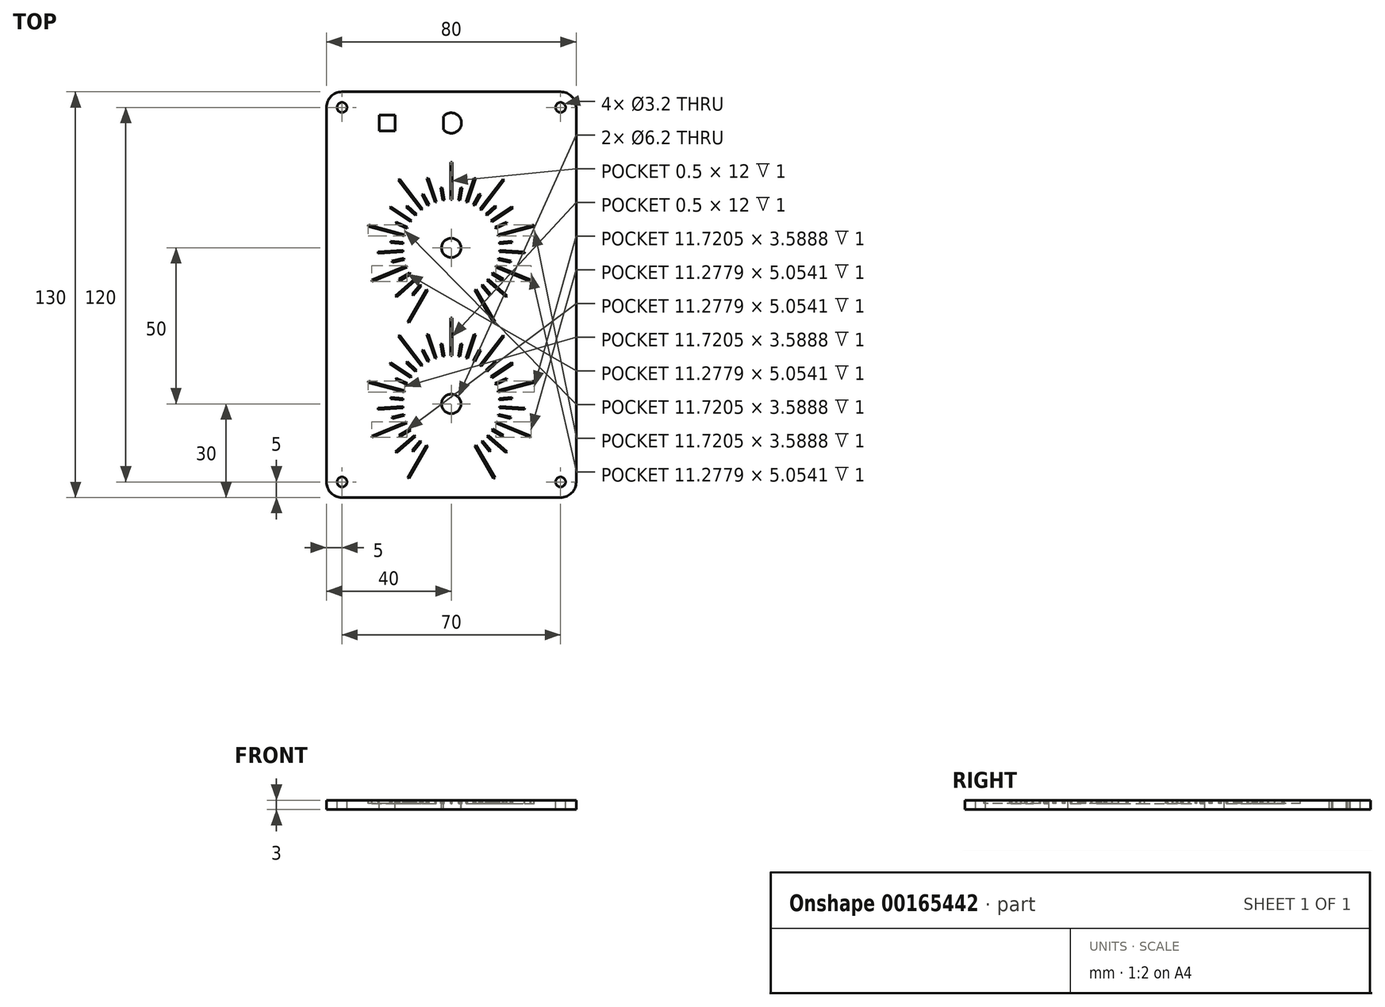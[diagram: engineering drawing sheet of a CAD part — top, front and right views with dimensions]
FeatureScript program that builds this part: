
annotation { "Feature Type Name" : "Feature", "Feature Type Description" : "" }
export const myFeature = defineFeature(function(context is Context, id is Id, definition is map)
    precondition{}
    {
        {
            var Q0;
            Q0=qCreatedBy(makeId("Top.planeOp"),FACE);
            var sketch = newSketch(context, id + "F0", { "sketchPlane" : qUnion([Q0])});
            skLineSegment(sketch, "E0.bottom", {"start": v(-35, 65) * mm, "end": v(35, 65) * mm});
            skLineSegment(sketch, "E0.top", {"start": v(-35, -65) * mm, "end": v(35, -65) * mm});
            skLineSegment(sketch, "E0.left", {"start": v(-40, 60) * mm, "end": v(-40, -60) * mm});
            skLineSegment(sketch, "E0.right", {"start": v(40, 60) * mm, "end": v(40, -60) * mm});
            skPoint(sketch, "E1", {"position": v(-40, 0) * mm});
            skPoint(sketch, "E2", {"position": v(0, 65) * mm});
            skPoint(sketch, "E3.visualSharp", {"position": v(-40, 65) * mm});
            skArc(sketch, "E3.filletArc", {"start": v(-35, 65) * mm, "mid": v(-38.54, 63.54) * mm, "end": v(-40, 60) * mm});
            skPoint(sketch, "E4.visualSharp", {"position": v(40, 65) * mm});
            skArc(sketch, "E4.filletArc", {"start": v(40, 60) * mm, "mid": v(38.54, 63.54) * mm, "end": v(35, 65) * mm});
            skPoint(sketch, "E5.visualSharp", {"position": v(-40, -65) * mm});
            skArc(sketch, "E5.filletArc", {"start": v(-40, -60) * mm, "mid": v(-38.54, -63.54) * mm, "end": v(-35, -65) * mm});
            skPoint(sketch, "E6.visualSharp", {"position": v(40, -65) * mm});
            skArc(sketch, "E6.filletArc", {"start": v(35, -65) * mm, "mid": v(38.54, -63.54) * mm, "end": v(40, -60) * mm});
            skSolve(sketch);
        }
        {
            var Q0;
            Q0=qSketchRegion(id+"F0",true);
            extrude(context, id + "F1", {"entities" : qUnion([Q0]), "depth" : 3 * mm});
        }
        {
            var Q0;
            Q0=makeQuery(id+"F1.opExtrude","CAP_FACE",FACE,{"disambiguationData":[OSD([sQuery(id+"F0.wireOp",EDGE,"E0.bottom"),sQuery(id+"F0.wireOp",EDGE,"E0.top"),sQuery(id+"F0.wireOp",EDGE,"E0.left"),sQuery(id+"F0.wireOp",EDGE,"E0.right"),sQuery(id+"F0.wireOp",EDGE,"E3.filletArc"),sQuery(id+"F0.wireOp",EDGE,"E4.filletArc"),sQuery(id+"F0.wireOp",EDGE,"E5.filletArc"),sQuery(id+"F0.wireOp",EDGE,"E6.filletArc")])],"isStart":false});
            var sketch = newSketch(context, id + "F2", { "sketchPlane" : qUnion([Q0])});
            skCircle(sketch, "E7", {"center": v(0, 15) * mm, "radius": 3.1 * mm});
            skCircle(sketch, "E8", {"center": v(0, -35) * mm, "radius": 3.1 * mm});
            skCircle(sketch, "E9", {"center": v(0, 15) * mm, "radius": 15.5 * mm, "construction": true});
            skCircle(sketch, "E10", {"center": v(0, -35) * mm, "radius": 15.5 * mm, "construction": true});
            skSolve(sketch);
        }
        {
            var Q0;
            Q0=qSketchRegion(id+"F2",true);
            extrude(context, id + "F3", {"entities" : qUnion([Q0]), "operationType" : NewBodyOperationType.REMOVE, "endBound" : BoundingType.THROUGH_ALL, "oppositeDirection" : true, "depth" : 25 * mm});
        }
        {
            var Q0;
            Q0=makeQuery(id+"F1.opExtrude","CAP_FACE",FACE,{"disambiguationData":[OSD([sQuery(id+"F0.wireOp",EDGE,"E0.bottom"),sQuery(id+"F0.wireOp",EDGE,"E0.top"),sQuery(id+"F0.wireOp",EDGE,"E0.left"),sQuery(id+"F0.wireOp",EDGE,"E0.right"),sQuery(id+"F0.wireOp",EDGE,"E3.filletArc"),sQuery(id+"F0.wireOp",EDGE,"E4.filletArc"),sQuery(id+"F0.wireOp",EDGE,"E5.filletArc"),sQuery(id+"F0.wireOp",EDGE,"E6.filletArc")])],"isStart":false});
            var sketch = newSketch(context, id + "F4", { "sketchPlane" : qUnion([Q0])});
            skLineSegment(sketch, "E11", {"start": v(0, 15) * mm, "end": v(0, -35) * mm, "construction": true});
            skCircle(sketch, "E12", {"center": v(-35, 60) * mm, "radius": 1.6 * mm});
            skCircle(sketch, "E13", {"center": v(35, 60) * mm, "radius": 1.6 * mm});
            skCircle(sketch, "E14", {"center": v(35, -60) * mm, "radius": 1.6 * mm});
            skCircle(sketch, "E15", {"center": v(-35, -60) * mm, "radius": 1.6 * mm});
            skSolve(sketch);
        }
        {
            var Q0;
            Q0=qSketchRegion(id+"F4",true);
            extrude(context, id + "F5", {"entities" : qUnion([Q0]), "operationType" : NewBodyOperationType.REMOVE, "endBound" : BoundingType.THROUGH_ALL, "oppositeDirection" : true, "depth" : 25 * mm});
        }
        {
            var Q0;
            Q0=makeQuery(id+"F2.imprint","IMPRINT",FACE,{"disambiguationData":[TD([[makeQuery(id+"F2.imprint","IMPRINT",EDGE,{"derivedFrom":sQuery(id+"F2.wireOp",EDGE,"E7")}),-1.0]])]});
            var sketch = newSketch(context, id + "F6", { "sketchPlane" : qUnion([Q0])});
            skArc(sketch, "E16", {"start": v(-2.46, 52.85) * mm, "mid": v(3.26, 55) * mm, "end": v(-2.46, 57.15) * mm});
            skLineSegment(sketch, "E17", {"start": v(-2.46, 57.15) * mm, "end": v(-2.46, 52.85) * mm});
            skLineSegment(sketch, "E18.bottom", {"start": v(-23.1, 57.55) * mm, "end": v(-18, 57.55) * mm});
            skLineSegment(sketch, "E18.top", {"start": v(-23.1, 52.45) * mm, "end": v(-18, 52.45) * mm});
            skLineSegment(sketch, "E18.left", {"start": v(-23.1, 57.55) * mm, "end": v(-23.1, 52.45) * mm});
            skLineSegment(sketch, "E18.right", {"start": v(-18, 57.55) * mm, "end": v(-18, 52.45) * mm});
            skPoint(sketch, "E19", {"position": v(-23.1, 55) * mm});
            skSolve(sketch);
        }
        {
            var Q0;
            Q0 = qSketchRegion(id + "F6", true);
            extrude(context, id + "F7", {"entities" : qUnion([Q0]), "operationType" : NewBodyOperationType.REMOVE, "endBound" : BoundingType.THROUGH_ALL, "oppositeDirection" : true, "depth" : 25 * mm});
        }
        {
            var Q0;
            Q0=makeQuery(id+"F2.imprint","IMPRINT",FACE,{"disambiguationData":[TD([[makeQuery(id+"F2.imprint","IMPRINT",EDGE,{"derivedFrom":sQuery(id+"F2.wireOp",EDGE,"E7")}),-1.0]])]});
            var sketch = newSketch(context, id + "F8", { "sketchPlane" : qUnion([Q0])});
            skLineSegment(sketch, "E20.bottom", {"start": v(-0.25, 34.5) * mm, "end": v(0.25, 34.5) * mm});
            skLineSegment(sketch, "E20.top", {"start": v(-0.25, 30.5) * mm, "end": v(0.25, 30.5) * mm});
            skLineSegment(sketch, "E20.left", {"start": v(-0.25, 34.5) * mm, "end": v(-0.25, 30.5) * mm});
            skLineSegment(sketch, "E20.right", {"start": v(0.25, 34.5) * mm, "end": v(0.25, 30.5) * mm});
            skLineSegment(sketch, "E21.top", {"start": v(-0.25, 38.5) * mm, "end": v(0.25, 38.5) * mm});
            skLineSegment(sketch, "E21.left", {"start": v(-0.25, 34.5) * mm, "end": v(-0.25, 38.5) * mm});
            skLineSegment(sketch, "E21.right", {"start": v(0.25, 34.5) * mm, "end": v(0.25, 38.5) * mm});
            skLineSegment(sketch, "E22.top", {"start": v(-0.25, 42.5) * mm, "end": v(0.25, 42.5) * mm});
            skLineSegment(sketch, "E22.left", {"start": v(-0.25, 38.5) * mm, "end": v(-0.25, 42.5) * mm});
            skLineSegment(sketch, "E22.right", {"start": v(0.25, 38.5) * mm, "end": v(0.25, 42.5) * mm});
            skPoint(sketch, "E23", {"position": v(0, 30.5) * mm});
            skLineSegment(sketch, "E24.1.0", {"start": v(14.1, 33.8) * mm, "end": v(16.54, 36.97) * mm});
            skLineSegment(sketch, "E24.1.1", {"start": v(16.54, 36.97) * mm, "end": v(16.94, 36.66) * mm});
            skLineSegment(sketch, "E24.1.2", {"start": v(14.1, 33.8) * mm, "end": v(14.5, 33.5) * mm});
            skLineSegment(sketch, "E24.1.3", {"start": v(14.5, 33.5) * mm, "end": v(16.94, 36.66) * mm});
            skLineSegment(sketch, "E24.1.4", {"start": v(14.1, 33.8) * mm, "end": v(14.5, 33.5) * mm});
            skLineSegment(sketch, "E24.2.0", {"start": v(22.63, 21.32) * mm, "end": v(26.5, 22.36) * mm});
            skLineSegment(sketch, "E24.2.1", {"start": v(26.5, 22.36) * mm, "end": v(26.63, 21.88) * mm});
            skLineSegment(sketch, "E24.2.2", {"start": v(22.63, 21.32) * mm, "end": v(22.76, 20.84) * mm});
            skLineSegment(sketch, "E24.2.3", {"start": v(22.76, 20.84) * mm, "end": v(26.63, 21.88) * mm});
            skLineSegment(sketch, "E24.2.4", {"start": v(22.63, 21.32) * mm, "end": v(22.76, 20.84) * mm});
            skPoint(sketch, "E24.center", {"position": v(0, 15) * mm});
            skLineSegment(sketch, "E24.anchor1", {"start": v(0, 15) * mm, "end": v(-0.25, 38.5) * mm, "construction": true});
            skLineSegment(sketch, "E24.anchor2", {"start": v(0, 15) * mm, "end": v(11.97, -5.22) * mm, "construction": true});
            skLineSegment(sketch, "E25.1.3.0", {"start": v(21.8, 6.24) * mm, "end": v(25.5, 4.7) * mm});
            skLineSegment(sketch, "E25.3.3.0", {"start": v(25.5, 4.7) * mm, "end": v(25.3, 4.25) * mm});
            skLineSegment(sketch, "E25.6.3.0", {"start": v(21.8, 6.24) * mm, "end": v(21.61, 5.78) * mm});
            skLineSegment(sketch, "E25.9.3.0", {"start": v(21.61, 5.78) * mm, "end": v(25.3, 4.25) * mm});
            skLineSegment(sketch, "E25.12.3.0", {"start": v(21.8, 6.24) * mm, "end": v(21.61, 5.78) * mm});
            skLineSegment(sketch, "E25.1.4.0", {"start": v(11.97, -5.22) * mm, "end": v(13.97, -8.69) * mm});
            skLineSegment(sketch, "E25.3.4.0", {"start": v(13.97, -8.69) * mm, "end": v(13.53, -8.94) * mm});
            skLineSegment(sketch, "E25.6.4.0", {"start": v(11.97, -5.22) * mm, "end": v(11.53, -5.47) * mm});
            skLineSegment(sketch, "E25.9.4.0", {"start": v(11.53, -5.47) * mm, "end": v(13.53, -8.94) * mm});
            skLineSegment(sketch, "E25.12.4.0", {"start": v(11.97, -5.22) * mm, "end": v(11.53, -5.47) * mm});
            skLineSegment(sketch, "E26.1.0", {"start": v(7.32, 37.33) * mm, "end": v(7.79, 37.17) * mm});
            skLineSegment(sketch, "E26.1.1", {"start": v(6.5, 33.38) * mm, "end": v(7.79, 37.17) * mm});
            skLineSegment(sketch, "E26.1.2", {"start": v(6.03, 33.54) * mm, "end": v(6.5, 33.38) * mm});
            skLineSegment(sketch, "E26.1.3", {"start": v(6.03, 33.54) * mm, "end": v(7.32, 37.33) * mm});
            skLineSegment(sketch, "E26.1.4", {"start": v(7.32, 37.33) * mm, "end": v(7.79, 37.17) * mm});
            skLineSegment(sketch, "E26.1.5", {"start": v(6.03, 33.54) * mm, "end": v(6.5, 33.38) * mm});
            skLineSegment(sketch, "E26.2.1", {"start": v(12.07, 30.32) * mm, "end": v(14.5, 33.5) * mm});
            skLineSegment(sketch, "E26.2.2", {"start": v(11.67, 30.62) * mm, "end": v(12.07, 30.32) * mm});
            skLineSegment(sketch, "E26.2.3", {"start": v(11.67, 30.62) * mm, "end": v(14.1, 33.8) * mm});
            skLineSegment(sketch, "E26.2.5", {"start": v(11.67, 30.62) * mm, "end": v(12.07, 30.32) * mm});
            skLineSegment(sketch, "E26.3.0", {"start": v(19.4, 28.26) * mm, "end": v(19.68, 27.85) * mm});
            skLineSegment(sketch, "E26.3.1", {"start": v(16.35, 25.62) * mm, "end": v(19.68, 27.85) * mm});
            skLineSegment(sketch, "E26.3.2", {"start": v(16.07, 26.04) * mm, "end": v(16.35, 25.62) * mm});
            skLineSegment(sketch, "E26.3.3", {"start": v(16.07, 26.04) * mm, "end": v(19.4, 28.26) * mm});
            skLineSegment(sketch, "E26.3.4", {"start": v(19.4, 28.26) * mm, "end": v(19.68, 27.85) * mm});
            skLineSegment(sketch, "E26.3.5", {"start": v(16.07, 26.04) * mm, "end": v(16.35, 25.62) * mm});
            skLineSegment(sketch, "E26.4.1", {"start": v(18.9, 19.8) * mm, "end": v(22.76, 20.84) * mm});
            skLineSegment(sketch, "E26.4.2", {"start": v(18.77, 20.29) * mm, "end": v(18.9, 19.8) * mm});
            skLineSegment(sketch, "E26.4.3", {"start": v(18.77, 20.29) * mm, "end": v(22.63, 21.32) * mm});
            skLineSegment(sketch, "E26.4.5", {"start": v(18.77, 20.29) * mm, "end": v(18.9, 19.8) * mm});
            skLineSegment(sketch, "E26.5.0", {"start": v(23.46, 13.71) * mm, "end": v(23.43, 13.21) * mm});
            skLineSegment(sketch, "E26.5.1", {"start": v(19.44, 13.48) * mm, "end": v(23.43, 13.21) * mm});
            skLineSegment(sketch, "E26.5.2", {"start": v(19.47, 13.97) * mm, "end": v(19.44, 13.48) * mm});
            skLineSegment(sketch, "E26.5.3", {"start": v(19.47, 13.97) * mm, "end": v(23.46, 13.71) * mm});
            skLineSegment(sketch, "E26.5.4", {"start": v(23.46, 13.71) * mm, "end": v(23.43, 13.21) * mm});
            skLineSegment(sketch, "E26.5.5", {"start": v(19.47, 13.97) * mm, "end": v(19.44, 13.48) * mm});
            skLineSegment(sketch, "E26.6.1", {"start": v(17.92, 7.3) * mm, "end": v(21.61, 5.78) * mm});
            skLineSegment(sketch, "E26.6.2", {"start": v(18.1, 7.77) * mm, "end": v(17.92, 7.3) * mm});
            skLineSegment(sketch, "E26.6.3", {"start": v(18.1, 7.77) * mm, "end": v(21.8, 6.24) * mm});
            skLineSegment(sketch, "E26.6.5", {"start": v(18.1, 7.77) * mm, "end": v(17.92, 7.3) * mm});
            skLineSegment(sketch, "E26.7.0", {"start": v(17.83, -0.3) * mm, "end": v(17.5, -0.68) * mm});
            skLineSegment(sketch, "E26.7.1", {"start": v(14.5, 1.96) * mm, "end": v(17.5, -0.68) * mm});
            skLineSegment(sketch, "E26.7.2", {"start": v(14.82, 2.33) * mm, "end": v(14.5, 1.96) * mm});
            skLineSegment(sketch, "E26.7.3", {"start": v(14.82, 2.33) * mm, "end": v(17.83, -0.3) * mm});
            skLineSegment(sketch, "E26.7.4", {"start": v(17.83, -0.3) * mm, "end": v(17.5, -0.68) * mm});
            skLineSegment(sketch, "E26.7.5", {"start": v(14.82, 2.33) * mm, "end": v(14.5, 1.96) * mm});
            skLineSegment(sketch, "E26.8.1", {"start": v(9.53, -2.01) * mm, "end": v(11.53, -5.47) * mm});
            skLineSegment(sketch, "E26.8.2", {"start": v(9.97, -1.76) * mm, "end": v(9.53, -2.01) * mm});
            skLineSegment(sketch, "E26.8.3", {"start": v(9.97, -1.76) * mm, "end": v(11.97, -5.22) * mm});
            skLineSegment(sketch, "E26.8.5", {"start": v(9.97, -1.76) * mm, "end": v(9.53, -2.01) * mm});
            skLineSegment(sketch, "E26.anchor1", {"start": v(0, 15) * mm, "end": v(-0.25, 34.5) * mm, "construction": true});
            skLineSegment(sketch, "E26.anchor2", {"start": v(0, 15) * mm, "end": v(9.97, -1.76) * mm, "construction": true});
            skPoint(sketch, "E27.1.0", {"position": v(2.52, 30.3) * mm});
            skLineSegment(sketch, "E27.1.1", {"start": v(3.42, 34.2) * mm, "end": v(2.77, 30.25) * mm});
            skLineSegment(sketch, "E27.1.2", {"start": v(2.93, 34.28) * mm, "end": v(3.42, 34.2) * mm});
            skLineSegment(sketch, "E27.1.3", {"start": v(2.93, 34.28) * mm, "end": v(2.28, 30.33) * mm});
            skLineSegment(sketch, "E27.1.4", {"start": v(2.93, 34.28) * mm, "end": v(3.42, 34.2) * mm});
            skLineSegment(sketch, "E27.1.5", {"start": v(2.28, 30.33) * mm, "end": v(2.77, 30.25) * mm});
            skPoint(sketch, "E27.2.0", {"position": v(4.98, 29.68) * mm});
            skLineSegment(sketch, "E27.2.1", {"start": v(6.5, 33.38) * mm, "end": v(5.22, 29.6) * mm});
            skLineSegment(sketch, "E27.2.3", {"start": v(6.03, 33.54) * mm, "end": v(4.74, 29.76) * mm});
            skLineSegment(sketch, "E27.2.5", {"start": v(4.74, 29.76) * mm, "end": v(5.22, 29.6) * mm});
            skPoint(sketch, "E27.3.0", {"position": v(7.3, 28.67) * mm});
            skLineSegment(sketch, "E27.3.1", {"start": v(9.41, 32.08) * mm, "end": v(7.53, 28.55) * mm});
            skLineSegment(sketch, "E27.3.2", {"start": v(8.97, 32.31) * mm, "end": v(9.41, 32.08) * mm});
            skLineSegment(sketch, "E27.3.3", {"start": v(8.97, 32.31) * mm, "end": v(7.09, 28.79) * mm});
            skLineSegment(sketch, "E27.3.4", {"start": v(8.97, 32.31) * mm, "end": v(9.41, 32.08) * mm});
            skLineSegment(sketch, "E27.3.5", {"start": v(7.09, 28.79) * mm, "end": v(7.53, 28.55) * mm});
            skPoint(sketch, "E27.4.0", {"position": v(9.43, 27.3) * mm});
            skLineSegment(sketch, "E27.4.1", {"start": v(12.07, 30.32) * mm, "end": v(9.63, 27.14) * mm});
            skLineSegment(sketch, "E27.4.3", {"start": v(11.67, 30.62) * mm, "end": v(9.24, 27.45) * mm});
            skLineSegment(sketch, "E27.4.5", {"start": v(9.24, 27.45) * mm, "end": v(9.63, 27.14) * mm});
            skPoint(sketch, "E27.5.0", {"position": v(11.31, 25.6) * mm});
            skLineSegment(sketch, "E27.5.1", {"start": v(14.4, 28.15) * mm, "end": v(11.48, 25.41) * mm});
            skLineSegment(sketch, "E27.5.2", {"start": v(14.06, 28.51) * mm, "end": v(14.4, 28.15) * mm});
            skLineSegment(sketch, "E27.5.3", {"start": v(14.06, 28.51) * mm, "end": v(11.14, 25.78) * mm});
            skLineSegment(sketch, "E27.5.4", {"start": v(14.06, 28.51) * mm, "end": v(14.4, 28.15) * mm});
            skLineSegment(sketch, "E27.5.5", {"start": v(11.14, 25.78) * mm, "end": v(11.48, 25.41) * mm});
            skPoint(sketch, "E27.6.0", {"position": v(12.89, 23.61) * mm});
            skLineSegment(sketch, "E27.6.1", {"start": v(16.35, 25.62) * mm, "end": v(13.02, 23.4) * mm});
            skLineSegment(sketch, "E27.6.3", {"start": v(16.07, 26.04) * mm, "end": v(12.75, 23.82) * mm});
            skLineSegment(sketch, "E27.6.5", {"start": v(12.75, 23.82) * mm, "end": v(13.02, 23.4) * mm});
            skPoint(sketch, "E27.7.0", {"position": v(14.12, 21.4) * mm});
            skLineSegment(sketch, "E27.7.1", {"start": v(17.86, 22.82) * mm, "end": v(14.22, 21.17) * mm});
            skLineSegment(sketch, "E27.7.2", {"start": v(17.66, 23.27) * mm, "end": v(17.86, 22.82) * mm});
            skLineSegment(sketch, "E27.7.3", {"start": v(17.66, 23.27) * mm, "end": v(14.01, 21.62) * mm});
            skLineSegment(sketch, "E27.7.4", {"start": v(17.66, 23.27) * mm, "end": v(17.86, 22.82) * mm});
            skLineSegment(sketch, "E27.7.5", {"start": v(14.01, 21.62) * mm, "end": v(14.22, 21.17) * mm});
            skPoint(sketch, "E27.8.0", {"position": v(14.97, 19.01) * mm});
            skLineSegment(sketch, "E27.8.1", {"start": v(18.9, 19.8) * mm, "end": v(15.03, 18.77) * mm});
            skLineSegment(sketch, "E27.8.3", {"start": v(18.77, 20.29) * mm, "end": v(14.9, 19.25) * mm});
            skLineSegment(sketch, "E27.8.5", {"start": v(14.9, 19.25) * mm, "end": v(15.03, 18.77) * mm});
            skPoint(sketch, "E27.9.0", {"position": v(15.42, 16.52) * mm});
            skLineSegment(sketch, "E27.9.1", {"start": v(19.43, 16.66) * mm, "end": v(15.45, 16.27) * mm});
            skLineSegment(sketch, "E27.9.2", {"start": v(19.38, 17.16) * mm, "end": v(19.43, 16.66) * mm});
            skLineSegment(sketch, "E27.9.3", {"start": v(19.38, 17.16) * mm, "end": v(15.4, 16.77) * mm});
            skLineSegment(sketch, "E27.9.4", {"start": v(19.38, 17.16) * mm, "end": v(19.43, 16.66) * mm});
            skLineSegment(sketch, "E27.9.5", {"start": v(15.4, 16.77) * mm, "end": v(15.45, 16.27) * mm});
            skPoint(sketch, "E27.10.0", {"position": v(15.46, 13.99) * mm});
            skLineSegment(sketch, "E27.10.1", {"start": v(19.44, 13.48) * mm, "end": v(15.45, 13.74) * mm});
            skLineSegment(sketch, "E27.10.3", {"start": v(19.47, 13.97) * mm, "end": v(15.48, 14.24) * mm});
            skLineSegment(sketch, "E27.10.5", {"start": v(15.48, 14.24) * mm, "end": v(15.45, 13.74) * mm});
            skPoint(sketch, "E27.11.0", {"position": v(15.1, 11.48) * mm});
            skLineSegment(sketch, "E27.11.1", {"start": v(18.93, 10.33) * mm, "end": v(15.04, 11.24) * mm});
            skLineSegment(sketch, "E27.11.2", {"start": v(19.05, 10.82) * mm, "end": v(18.93, 10.33) * mm});
            skLineSegment(sketch, "E27.11.3", {"start": v(19.05, 10.82) * mm, "end": v(15.15, 11.72) * mm});
            skLineSegment(sketch, "E27.11.4", {"start": v(19.05, 10.82) * mm, "end": v(18.93, 10.33) * mm});
            skLineSegment(sketch, "E27.11.5", {"start": v(15.15, 11.72) * mm, "end": v(15.04, 11.24) * mm});
            skPoint(sketch, "E27.12.0", {"position": v(14.32, 9.07) * mm});
            skLineSegment(sketch, "E27.12.1", {"start": v(17.92, 7.3) * mm, "end": v(14.22, 8.84) * mm});
            skLineSegment(sketch, "E27.12.3", {"start": v(18.1, 7.77) * mm, "end": v(14.41, 9.3) * mm});
            skLineSegment(sketch, "E27.12.5", {"start": v(14.41, 9.3) * mm, "end": v(14.22, 8.84) * mm});
            skPoint(sketch, "E27.13.0", {"position": v(13.16, 6.82) * mm});
            skLineSegment(sketch, "E27.13.1", {"start": v(16.43, 4.5) * mm, "end": v(13.03, 6.6) * mm});
            skLineSegment(sketch, "E27.13.2", {"start": v(16.69, 4.92) * mm, "end": v(16.43, 4.5) * mm});
            skLineSegment(sketch, "E27.13.3", {"start": v(16.69, 4.92) * mm, "end": v(13.3, 7.03) * mm});
            skLineSegment(sketch, "E27.13.4", {"start": v(16.69, 4.92) * mm, "end": v(16.43, 4.5) * mm});
            skLineSegment(sketch, "E27.13.5", {"start": v(13.3, 7.03) * mm, "end": v(13.03, 6.6) * mm});
            skPoint(sketch, "E27.14.0", {"position": v(11.65, 4.78) * mm});
            skLineSegment(sketch, "E27.14.1", {"start": v(14.5, 1.96) * mm, "end": v(11.49, 4.6) * mm});
            skLineSegment(sketch, "E27.14.3", {"start": v(14.82, 2.33) * mm, "end": v(11.82, 4.97) * mm});
            skLineSegment(sketch, "E27.14.5", {"start": v(11.82, 4.97) * mm, "end": v(11.49, 4.6) * mm});
            skPoint(sketch, "E27.15.0", {"position": v(9.83, 3.02) * mm});
            skLineSegment(sketch, "E27.15.1", {"start": v(12.18, -0.23) * mm, "end": v(9.64, 2.86) * mm});
            skLineSegment(sketch, "E27.15.2", {"start": v(12.56, 0.09) * mm, "end": v(12.18, -0.23) * mm});
            skLineSegment(sketch, "E27.15.3", {"start": v(12.56, 0.09) * mm, "end": v(10.03, 3.18) * mm});
            skLineSegment(sketch, "E27.15.4", {"start": v(12.56, 0.09) * mm, "end": v(12.18, -0.23) * mm});
            skLineSegment(sketch, "E27.15.5", {"start": v(10.03, 3.18) * mm, "end": v(9.64, 2.86) * mm});
            skLineSegment(sketch, "E27.anchor1", {"start": v(0, 15) * mm, "end": v(-0.25, 30.5) * mm, "construction": true});
            skLineSegment(sketch, "E27.anchor2", {"start": v(0, 15) * mm, "end": v(7.97, 1.7) * mm, "construction": true});
            skLineSegment(sketch, "E28.1.16.0", {"start": v(9.53, -2.01) * mm, "end": v(7.53, 1.45) * mm});
            skLineSegment(sketch, "E28.7.16.0", {"start": v(9.97, -1.76) * mm, "end": v(7.97, 1.7) * mm});
            skPoint(sketch, "E28.9.16.0", {"position": v(7.75, 1.58) * mm});
            skLineSegment(sketch, "E28.13.16.0", {"start": v(7.97, 1.7) * mm, "end": v(7.53, 1.45) * mm});
            skLineSegment(sketch, "E29.MirrorCS", {"start": v(-9.97, -1.76) * mm, "end": v(-9.53, -2.01) * mm});
            skLineSegment(sketch, "E30.MirrorCS", {"start": v(-11.97, -5.22) * mm, "end": v(-11.53, -5.47) * mm});
            skLineSegment(sketch, "E31.MirrorCS", {"start": v(-18.1, 7.77) * mm, "end": v(-17.92, 7.3) * mm});
            skLineSegment(sketch, "E32.MirrorCS", {"start": v(-19.47, 13.97) * mm, "end": v(-19.44, 13.48) * mm});
            skLineSegment(sketch, "E33.MirrorCS", {"start": v(-14.1, 33.8) * mm, "end": v(-14.5, 33.5) * mm});
            skLineSegment(sketch, "E34.MirrorCS", {"start": v(-16.07, 26.04) * mm, "end": v(-16.35, 25.62) * mm});
            skLineSegment(sketch, "E35.MirrorCS", {"start": v(-22.63, 21.32) * mm, "end": v(-22.76, 20.84) * mm});
            skLineSegment(sketch, "E36.MirrorCS", {"start": v(-6.03, 33.54) * mm, "end": v(-6.5, 33.38) * mm});
            skLineSegment(sketch, "E37.MirrorCS", {"start": v(-14.82, 2.33) * mm, "end": v(-14.5, 1.96) * mm});
            skLineSegment(sketch, "E38.MirrorCS", {"start": v(-18.77, 20.29) * mm, "end": v(-18.9, 19.8) * mm});
            skLineSegment(sketch, "E39.MirrorCS", {"start": v(-21.8, 6.24) * mm, "end": v(-21.61, 5.78) * mm});
            skLineSegment(sketch, "E40.MirrorCS", {"start": v(-11.67, 30.62) * mm, "end": v(-12.07, 30.32) * mm});
            skLineSegment(sketch, "E41.MirrorCS", {"start": v(-7.32, 37.33) * mm, "end": v(-7.79, 37.17) * mm});
            skLineSegment(sketch, "E42.MirrorCS", {"start": v(-19.4, 28.26) * mm, "end": v(-19.68, 27.85) * mm});
            skLineSegment(sketch, "E43.MirrorCS", {"start": v(-16.69, 4.92) * mm, "end": v(-16.43, 4.5) * mm});
            skLineSegment(sketch, "E44.MirrorCS", {"start": v(-12.56, 0.09) * mm, "end": v(-12.18, -0.23) * mm});
            skLineSegment(sketch, "E45.MirrorCS", {"start": v(-19.38, 17.16) * mm, "end": v(-19.43, 16.66) * mm});
            skLineSegment(sketch, "E46.MirrorCS", {"start": v(-15.4, 16.77) * mm, "end": v(-15.45, 16.27) * mm});
            skLineSegment(sketch, "E47.MirrorCS", {"start": v(-23.46, 13.71) * mm, "end": v(-23.43, 13.21) * mm});
            skLineSegment(sketch, "E48.MirrorCS", {"start": v(-14.06, 28.51) * mm, "end": v(-14.4, 28.15) * mm});
            skLineSegment(sketch, "E49.MirrorCS", {"start": v(-17.66, 23.27) * mm, "end": v(-17.86, 22.82) * mm});
            skLineSegment(sketch, "E50.MirrorCS", {"start": v(-7.97, 1.7) * mm, "end": v(-7.53, 1.45) * mm});
            skLineSegment(sketch, "E51.MirrorCS", {"start": v(-17.83, -0.3) * mm, "end": v(-17.5, -0.68) * mm});
            skLineSegment(sketch, "E52.MirrorCS", {"start": v(-2.93, 34.28) * mm, "end": v(-3.42, 34.2) * mm});
            skLineSegment(sketch, "E53.MirrorCS", {"start": v(-15.48, 14.24) * mm, "end": v(-15.45, 13.74) * mm});
            skLineSegment(sketch, "E54.MirrorCS", {"start": v(-8.97, 32.31) * mm, "end": v(-9.41, 32.08) * mm});
            skLineSegment(sketch, "E55.MirrorCS", {"start": v(-19.05, 10.82) * mm, "end": v(-18.93, 10.33) * mm});
            skLineSegment(sketch, "E56.MirrorCS", {"start": v(-2.28, 30.33) * mm, "end": v(-2.77, 30.25) * mm});
            skLineSegment(sketch, "E57.MirrorCS", {"start": v(-7.09, 28.79) * mm, "end": v(-7.53, 28.55) * mm});
            skLineSegment(sketch, "E58.MirrorCS", {"start": v(-12.75, 23.82) * mm, "end": v(-13.02, 23.4) * mm});
            skLineSegment(sketch, "E59.MirrorCS", {"start": v(-15.15, 11.72) * mm, "end": v(-15.04, 11.24) * mm});
            skLineSegment(sketch, "E60.MirrorCS", {"start": v(-10.03, 3.18) * mm, "end": v(-9.64, 2.86) * mm});
            skLineSegment(sketch, "E61.MirrorCS", {"start": v(-11.82, 4.97) * mm, "end": v(-11.49, 4.6) * mm});
            skLineSegment(sketch, "E62.MirrorCS", {"start": v(-4.74, 29.76) * mm, "end": v(-5.22, 29.6) * mm});
            skLineSegment(sketch, "E63.MirrorCS", {"start": v(-11.14, 25.78) * mm, "end": v(-11.48, 25.41) * mm});
            skLineSegment(sketch, "E64.MirrorCS", {"start": v(-13.3, 7.03) * mm, "end": v(-13.03, 6.6) * mm});
            skLineSegment(sketch, "E65.MirrorCS", {"start": v(-14.9, 19.25) * mm, "end": v(-15.03, 18.77) * mm});
            skLineSegment(sketch, "E66.MirrorCS", {"start": v(-14.41, 9.3) * mm, "end": v(-14.22, 8.84) * mm});
            skLineSegment(sketch, "E67.MirrorCS", {"start": v(-14.01, 21.62) * mm, "end": v(-14.22, 21.17) * mm});
            skLineSegment(sketch, "E68.MirrorCS", {"start": v(-9.24, 27.45) * mm, "end": v(-9.63, 27.14) * mm});
            skLineSegment(sketch, "E69.MirrorCS", {"start": v(-26.5, 22.36) * mm, "end": v(-26.63, 21.88) * mm});
            skLineSegment(sketch, "E70.MirrorCS", {"start": v(-16.54, 36.97) * mm, "end": v(-16.94, 36.66) * mm});
            skLineSegment(sketch, "E71.MirrorCS", {"start": v(-25.5, 4.7) * mm, "end": v(-25.3, 4.25) * mm});
            skLineSegment(sketch, "E72.MirrorCS", {"start": v(-13.97, -8.69) * mm, "end": v(-13.53, -8.94) * mm});
            skLineSegment(sketch, "E73.MirrorCS", {"start": v(-16.69, 4.92) * mm, "end": v(-13.3, 7.03) * mm});
            skLineSegment(sketch, "E74.MirrorCS", {"start": v(-17.86, 22.82) * mm, "end": v(-14.22, 21.17) * mm});
            skPoint(sketch, "E75.MirrorP", {"position": v(-9.43, 27.3) * mm});
            skLineSegment(sketch, "E76.MirrorCS", {"start": v(-14.5, 33.5) * mm, "end": v(-16.94, 36.66) * mm});
            skLineSegment(sketch, "E77.MirrorCS", {"start": v(-12.07, 30.32) * mm, "end": v(-9.63, 27.14) * mm});
            skLineSegment(sketch, "E78.MirrorCS", {"start": v(-18.1, 7.77) * mm, "end": v(-21.8, 6.24) * mm});
            skLineSegment(sketch, "E79.MirrorCS", {"start": v(-9.97, -1.76) * mm, "end": v(-7.97, 1.7) * mm});
            skLineSegment(sketch, "E80.MirrorCS", {"start": v(-9.53, -2.01) * mm, "end": v(-11.53, -5.47) * mm});
            skLineSegment(sketch, "E81.MirrorCS", {"start": v(-8.97, 32.31) * mm, "end": v(-7.09, 28.79) * mm});
            skLineSegment(sketch, "E82.MirrorCS", {"start": v(-16.07, 26.04) * mm, "end": v(-19.4, 28.26) * mm});
            skLineSegment(sketch, "E83.MirrorCS", {"start": v(-12.07, 30.32) * mm, "end": v(-14.5, 33.5) * mm});
            skLineSegment(sketch, "E84.MirrorCS", {"start": v(-14.82, 2.33) * mm, "end": v(-17.83, -0.3) * mm});
            skLineSegment(sketch, "E85.MirrorCS", {"start": v(-19.47, 13.97) * mm, "end": v(-23.46, 13.71) * mm});
            skPoint(sketch, "E86.MirrorP", {"position": v(-4.98, 29.68) * mm});
            skLineSegment(sketch, "E87.MirrorCS", {"start": v(-17.92, 7.3) * mm, "end": v(-21.61, 5.78) * mm});
            skPoint(sketch, "E88.MirrorP", {"position": v(-13.16, 6.82) * mm});
            skLineSegment(sketch, "E89.MirrorCS", {"start": v(-14.06, 28.51) * mm, "end": v(-11.14, 25.78) * mm});
            skPoint(sketch, "E90.MirrorP", {"position": v(-9.83, 3.02) * mm});
            skLineSegment(sketch, "E91.MirrorCS", {"start": v(-16.35, 25.62) * mm, "end": v(-13.02, 23.4) * mm});
            skLineSegment(sketch, "E92.MirrorCS", {"start": v(-19.44, 13.48) * mm, "end": v(-15.45, 13.74) * mm});
            skLineSegment(sketch, "E93.MirrorCS", {"start": v(-18.1, 7.77) * mm, "end": v(-14.41, 9.3) * mm});
            skLineSegment(sketch, "E94.MirrorCS", {"start": v(-12.18, -0.23) * mm, "end": v(-9.64, 2.86) * mm});
            skLineSegment(sketch, "E95.MirrorCS", {"start": v(-19.43, 16.66) * mm, "end": v(-15.45, 16.27) * mm});
            skLineSegment(sketch, "E96.MirrorCS", {"start": v(-9.53, -2.01) * mm, "end": v(-7.53, 1.45) * mm});
            skLineSegment(sketch, "E97.MirrorCS", {"start": v(-19.38, 17.16) * mm, "end": v(-15.4, 16.77) * mm});
            skLineSegment(sketch, "E98.MirrorCS", {"start": v(-11.53, -5.47) * mm, "end": v(-13.53, -8.94) * mm});
            skLineSegment(sketch, "E99.MirrorCS", {"start": v(-9.41, 32.08) * mm, "end": v(-7.53, 28.55) * mm});
            skLineSegment(sketch, "E100.MirrorCS", {"start": v(-6.5, 33.38) * mm, "end": v(-5.22, 29.6) * mm});
            skLineSegment(sketch, "E101.MirrorCS", {"start": v(-18.77, 20.29) * mm, "end": v(-14.9, 19.25) * mm});
            skLineSegment(sketch, "E102.MirrorCS", {"start": v(-16.43, 4.5) * mm, "end": v(-13.03, 6.6) * mm});
            skPoint(sketch, "E103.MirrorP", {"position": v(-14.32, 9.07) * mm});
            skLineSegment(sketch, "E104.MirrorCS", {"start": v(-11.97, -5.22) * mm, "end": v(-13.97, -8.69) * mm});
            skLineSegment(sketch, "E105.MirrorCS", {"start": v(-3.42, 34.2) * mm, "end": v(-2.77, 30.25) * mm});
            skLineSegment(sketch, "E106.MirrorCS", {"start": v(-18.77, 20.29) * mm, "end": v(-22.63, 21.32) * mm});
            skLineSegment(sketch, "E107.MirrorCS", {"start": v(-19.05, 10.82) * mm, "end": v(-15.15, 11.72) * mm});
            skLineSegment(sketch, "E108.MirrorCS", {"start": v(-11.67, 30.62) * mm, "end": v(-9.24, 27.45) * mm});
            skLineSegment(sketch, "E109.MirrorCS", {"start": v(-18.93, 10.33) * mm, "end": v(-15.04, 11.24) * mm});
            skLineSegment(sketch, "E110.MirrorCS", {"start": v(-17.92, 7.3) * mm, "end": v(-14.22, 8.84) * mm});
            skPoint(sketch, "E111.MirrorP", {"position": v(-15.42, 16.52) * mm});
            skLineSegment(sketch, "E112.MirrorCS", {"start": v(-19.47, 13.97) * mm, "end": v(-15.48, 14.24) * mm});
            skLineSegment(sketch, "E113.MirrorCS", {"start": v(-14.82, 2.33) * mm, "end": v(-11.82, 4.97) * mm});
            skLineSegment(sketch, "E114.MirrorCS", {"start": v(-6.03, 33.54) * mm, "end": v(-4.74, 29.76) * mm});
            skLineSegment(sketch, "E115.MirrorCS", {"start": v(-14.5, 1.96) * mm, "end": v(-11.49, 4.6) * mm});
            skLineSegment(sketch, "E116.MirrorCS", {"start": v(-2.93, 34.28) * mm, "end": v(-2.28, 30.33) * mm});
            skLineSegment(sketch, "E117.MirrorCS", {"start": v(-6.5, 33.38) * mm, "end": v(-7.79, 37.17) * mm});
            skLineSegment(sketch, "E118.MirrorCS", {"start": v(-18.9, 19.8) * mm, "end": v(-22.76, 20.84) * mm});
            skLineSegment(sketch, "E119.MirrorCS", {"start": v(-21.8, 6.24) * mm, "end": v(-25.5, 4.7) * mm});
            skLineSegment(sketch, "E120.MirrorCS", {"start": v(-14.4, 28.15) * mm, "end": v(-11.48, 25.41) * mm});
            skPoint(sketch, "E121.MirrorP", {"position": v(-7.3, 28.67) * mm});
            skLineSegment(sketch, "E122.MirrorCS", {"start": v(-12.56, 0.09) * mm, "end": v(-10.03, 3.18) * mm});
            skLineSegment(sketch, "E123.MirrorCS", {"start": v(-16.07, 26.04) * mm, "end": v(-12.75, 23.82) * mm});
            skLineSegment(sketch, "E124.MirrorCS", {"start": v(-9.97, -1.76) * mm, "end": v(-11.97, -5.22) * mm});
            skPoint(sketch, "E125.MirrorP", {"position": v(-15.46, 13.99) * mm});
            skPoint(sketch, "E126.MirrorP", {"position": v(-12.89, 23.61) * mm});
            skPoint(sketch, "E127.MirrorP", {"position": v(-2.52, 30.3) * mm});
            skPoint(sketch, "E128.MirrorP", {"position": v(-15.1, 11.48) * mm});
            skLineSegment(sketch, "E129.MirrorCS", {"start": v(-22.76, 20.84) * mm, "end": v(-26.63, 21.88) * mm});
            skPoint(sketch, "E130.MirrorP", {"position": v(-7.75, 1.58) * mm});
            skLineSegment(sketch, "E131.MirrorCS", {"start": v(-11.67, 30.62) * mm, "end": v(-14.1, 33.8) * mm});
            skLineSegment(sketch, "E132.MirrorCS", {"start": v(-17.66, 23.27) * mm, "end": v(-14.01, 21.62) * mm});
            skLineSegment(sketch, "E133.MirrorCS", {"start": v(-14.5, 1.96) * mm, "end": v(-17.5, -0.68) * mm});
            skLineSegment(sketch, "E134.MirrorCS", {"start": v(-18.9, 19.8) * mm, "end": v(-15.03, 18.77) * mm});
            skLineSegment(sketch, "E135.MirrorCS", {"start": v(-22.63, 21.32) * mm, "end": v(-26.5, 22.36) * mm});
            skLineSegment(sketch, "E136.MirrorCS", {"start": v(-19.44, 13.48) * mm, "end": v(-23.43, 13.21) * mm});
            skLineSegment(sketch, "E137.MirrorCS", {"start": v(-6.03, 33.54) * mm, "end": v(-7.32, 37.33) * mm});
            skLineSegment(sketch, "E138.MirrorCS", {"start": v(-21.61, 5.78) * mm, "end": v(-25.3, 4.25) * mm});
            skPoint(sketch, "E139.MirrorP", {"position": v(-11.31, 25.6) * mm});
            skPoint(sketch, "E140.MirrorP", {"position": v(-11.65, 4.78) * mm});
            skLineSegment(sketch, "E141.MirrorCS", {"start": v(-16.35, 25.62) * mm, "end": v(-19.68, 27.85) * mm});
            skLineSegment(sketch, "E142.MirrorCS", {"start": v(-14.1, 33.8) * mm, "end": v(-16.54, 36.97) * mm});
            skPoint(sketch, "E143.MirrorP", {"position": v(-14.97, 19.01) * mm});
            skPoint(sketch, "E144.MirrorP", {"position": v(-14.12, 21.4) * mm});
            skPoint(sketch, "E145.0.1.0", {"position": v(15.1, -38.52) * mm});
            skPoint(sketch, "E145.0.1.1", {"position": v(-12.89, -26.39) * mm});
            skPoint(sketch, "E145.0.1.2", {"position": v(15.46, -36.01) * mm});
            skPoint(sketch, "E145.0.1.3", {"position": v(14.32, -40.93) * mm});
            skPoint(sketch, "E145.0.1.4", {"position": v(-15.1, -38.52) * mm});
            skLineSegment(sketch, "E145.0.1.5", {"start": v(0, -35) * mm, "end": v(11.97, -55.22) * mm, "construction": true});
            skPoint(sketch, "E145.0.1.6", {"position": v(15.42, -33.48) * mm});
            skPoint(sketch, "E145.0.1.7", {"position": v(-15.46, -36.01) * mm});
            skPoint(sketch, "E145.0.1.8", {"position": v(-7.3, -21.33) * mm});
            skPoint(sketch, "E145.0.1.9", {"position": v(14.97, -30.99) * mm});
            skPoint(sketch, "E145.0.1.10", {"position": v(14.12, -28.6) * mm});
            skPoint(sketch, "E145.0.1.11", {"position": v(-15.42, -33.48) * mm});
            skPoint(sketch, "E145.0.1.12", {"position": v(-14.32, -40.93) * mm});
            skPoint(sketch, "E145.0.1.13", {"position": v(12.89, -26.39) * mm});
            skPoint(sketch, "E145.0.1.14", {"position": v(-9.83, -46.98) * mm});
            skPoint(sketch, "E145.0.1.15", {"position": v(11.31, -24.4) * mm});
            skPoint(sketch, "E145.0.1.16", {"position": v(11.65, -45.22) * mm});
            skPoint(sketch, "E145.0.1.17", {"position": v(13.16, -43.18) * mm});
            skPoint(sketch, "E145.0.1.18", {"position": v(-11.65, -45.22) * mm});
            skPoint(sketch, "E145.0.1.19", {"position": v(-11.31, -24.4) * mm});
            skPoint(sketch, "E145.0.1.20", {"position": v(0, -35) * mm});
            skPoint(sketch, "E145.0.1.21", {"position": v(-14.97, -30.99) * mm});
            skPoint(sketch, "E145.0.1.22", {"position": v(2.52, -19.7) * mm});
            skPoint(sketch, "E145.0.1.23", {"position": v(-14.12, -28.6) * mm});
            skPoint(sketch, "E145.0.1.24", {"position": v(7.75, -48.42) * mm});
            skPoint(sketch, "E145.0.1.25", {"position": v(4.98, -20.32) * mm});
            skLineSegment(sketch, "E145.0.1.26", {"start": v(0, -35) * mm, "end": v(-0.25, -19.5) * mm, "construction": true});
            skPoint(sketch, "E145.0.1.27", {"position": v(-9.43, -22.7) * mm});
            skLineSegment(sketch, "E145.0.1.28", {"start": v(0, -35) * mm, "end": v(7.97, -48.3) * mm, "construction": true});
            skPoint(sketch, "E145.0.1.29", {"position": v(7.3, -21.33) * mm});
            skPoint(sketch, "E145.0.1.30", {"position": v(-4.98, -20.32) * mm});
            skPoint(sketch, "E145.0.1.31", {"position": v(9.43, -22.7) * mm});
            skPoint(sketch, "E145.0.1.32", {"position": v(-13.16, -43.18) * mm});
            skPoint(sketch, "E145.0.1.33", {"position": v(-7.75, -48.42) * mm});
            skPoint(sketch, "E145.0.1.34", {"position": v(9.83, -46.98) * mm});
            skPoint(sketch, "E145.0.1.35", {"position": v(0, -19.5) * mm});
            skPoint(sketch, "E145.0.1.36", {"position": v(-15.1, -38.52) * mm});
            skPoint(sketch, "E145.0.1.37", {"position": v(-2.52, -19.7) * mm});
            skPoint(sketch, "E145.0.1.38", {"position": v(-12.89, -26.39) * mm});
            skPoint(sketch, "E145.0.1.39", {"position": v(-7.75, -48.42) * mm});
            skPoint(sketch, "E145.0.1.40", {"position": v(-15.46, -36.01) * mm});
            skLineSegment(sketch, "E145.0.1.41", {"start": v(0, -35) * mm, "end": v(-0.25, -11.5) * mm, "construction": true});
            skPoint(sketch, "E145.0.1.42", {"position": v(-7.3, -21.33) * mm});
            skPoint(sketch, "E145.0.1.43", {"position": v(-15.42, -33.48) * mm});
            skPoint(sketch, "E145.0.1.44", {"position": v(-14.32, -40.93) * mm});
            skLineSegment(sketch, "E145.0.1.45", {"start": v(0, -35) * mm, "end": v(9.97, -51.76) * mm, "construction": true});
            skPoint(sketch, "E145.0.1.46", {"position": v(-9.83, -46.98) * mm});
            skPoint(sketch, "E145.0.1.47", {"position": v(-11.31, -24.4) * mm});
            skPoint(sketch, "E145.0.1.48", {"position": v(-11.65, -45.22) * mm});
            skPoint(sketch, "E145.0.1.49", {"position": v(0, -35) * mm});
            skPoint(sketch, "E145.0.1.50", {"position": v(-14.12, -28.6) * mm});
            skPoint(sketch, "E145.0.1.51", {"position": v(-9.43, -22.7) * mm});
            skPoint(sketch, "E145.0.1.52", {"position": v(-4.98, -20.32) * mm});
            skPoint(sketch, "E145.0.1.53", {"position": v(-13.16, -43.18) * mm});
            skPoint(sketch, "E145.0.1.54", {"position": v(-14.97, -30.99) * mm});
            skLineSegment(sketch, "E145.0.1.55", {"start": v(21.8, -43.76) * mm, "end": v(25.5, -45.3) * mm});
            skLineSegment(sketch, "E145.0.1.56", {"start": v(25.5, -45.3) * mm, "end": v(25.3, -45.75) * mm});
            skLineSegment(sketch, "E145.0.1.57", {"start": v(22.76, -29.16) * mm, "end": v(26.63, -28.12) * mm});
            skLineSegment(sketch, "E145.0.1.58", {"start": v(14.1, -16.2) * mm, "end": v(16.54, -13.03) * mm});
            skLineSegment(sketch, "E145.0.1.59", {"start": v(-0.25, -7.5) * mm, "end": v(0.25, -7.5) * mm});
            skLineSegment(sketch, "E145.0.1.60", {"start": v(0.25, -11.5) * mm, "end": v(0.25, -7.5) * mm});
            skLineSegment(sketch, "E145.0.1.61", {"start": v(-0.25, -11.5) * mm, "end": v(-0.25, -7.5) * mm});
            skLineSegment(sketch, "E145.0.1.62", {"start": v(14.5, -16.5) * mm, "end": v(16.94, -13.34) * mm});
            skLineSegment(sketch, "E145.0.1.63", {"start": v(0, -35) * mm, "end": v(-0.25, -15.5) * mm, "construction": true});
            skLineSegment(sketch, "E145.0.1.64", {"start": v(21.61, -44.22) * mm, "end": v(25.3, -45.75) * mm});
            skLineSegment(sketch, "E145.0.1.65", {"start": v(11.97, -55.22) * mm, "end": v(13.97, -58.69) * mm});
            skLineSegment(sketch, "E145.0.1.66", {"start": v(11.53, -55.47) * mm, "end": v(13.53, -58.94) * mm});
            skLineSegment(sketch, "E145.0.1.67", {"start": v(22.63, -28.68) * mm, "end": v(26.5, -27.64) * mm});
            skPoint(sketch, "E145.0.1.68", {"position": v(0, -35) * mm});
            skLineSegment(sketch, "E145.0.1.69", {"start": v(14.82, -47.67) * mm, "end": v(17.83, -50.3) * mm});
            skLineSegment(sketch, "E145.0.1.70", {"start": v(17.83, -50.3) * mm, "end": v(17.5, -50.68) * mm});
            skLineSegment(sketch, "E145.0.1.71", {"start": v(14.82, -47.67) * mm, "end": v(11.82, -45.03) * mm});
            skLineSegment(sketch, "E145.0.1.72", {"start": v(14.5, -48.04) * mm, "end": v(17.5, -50.68) * mm});
            skLineSegment(sketch, "E145.0.1.73", {"start": v(7.32, -12.67) * mm, "end": v(7.79, -12.83) * mm});
            skLineSegment(sketch, "E145.0.1.74", {"start": v(11.67, -19.38) * mm, "end": v(9.24, -22.55) * mm});
            skLineSegment(sketch, "E145.0.1.75", {"start": v(6.03, -16.46) * mm, "end": v(7.32, -12.67) * mm});
            skLineSegment(sketch, "E145.0.1.76", {"start": v(6.5, -16.62) * mm, "end": v(7.79, -12.83) * mm});
            skLineSegment(sketch, "E145.0.1.77", {"start": v(16.54, -13.03) * mm, "end": v(16.94, -13.34) * mm});
            skLineSegment(sketch, "E145.0.1.78", {"start": v(26.5, -27.64) * mm, "end": v(26.63, -28.12) * mm});
            skLineSegment(sketch, "E145.0.1.79", {"start": v(19.44, -36.52) * mm, "end": v(23.43, -36.79) * mm});
            skLineSegment(sketch, "E145.0.1.80", {"start": v(17.92, -42.7) * mm, "end": v(14.22, -41.16) * mm});
            skLineSegment(sketch, "E145.0.1.81", {"start": v(18.1, -42.23) * mm, "end": v(14.41, -40.7) * mm});
            skLineSegment(sketch, "E145.0.1.82", {"start": v(19.47, -36.03) * mm, "end": v(23.46, -36.29) * mm});
            skLineSegment(sketch, "E145.0.1.83", {"start": v(13.97, -58.69) * mm, "end": v(13.53, -58.94) * mm});
            skLineSegment(sketch, "E145.0.1.84", {"start": v(9.41, -17.92) * mm, "end": v(7.53, -21.45) * mm});
            skLineSegment(sketch, "E145.0.1.85", {"start": v(23.46, -36.29) * mm, "end": v(23.43, -36.79) * mm});
            skLineSegment(sketch, "E145.0.1.86", {"start": v(16.35, -24.38) * mm, "end": v(19.68, -22.15) * mm});
            skLineSegment(sketch, "E145.0.1.87", {"start": v(16.07, -23.96) * mm, "end": v(12.75, -26.18) * mm});
            skLineSegment(sketch, "E145.0.1.88", {"start": v(14.41, -40.7) * mm, "end": v(14.22, -41.16) * mm});
            skLineSegment(sketch, "E145.0.1.89", {"start": v(8.97, -17.69) * mm, "end": v(7.09, -21.21) * mm});
            skLineSegment(sketch, "E145.0.1.90", {"start": v(16.43, -45.5) * mm, "end": v(13.03, -43.4) * mm});
            skLineSegment(sketch, "E145.0.1.91", {"start": v(16.07, -23.96) * mm, "end": v(19.4, -21.74) * mm});
            skLineSegment(sketch, "E145.0.1.92", {"start": v(19.05, -39.18) * mm, "end": v(18.93, -39.67) * mm});
            skLineSegment(sketch, "E145.0.1.93", {"start": v(19.05, -39.18) * mm, "end": v(15.15, -38.28) * mm});
            skLineSegment(sketch, "E145.0.1.94", {"start": v(14.4, -21.85) * mm, "end": v(11.48, -24.59) * mm});
            skLineSegment(sketch, "E145.0.1.95", {"start": v(6.5, -16.62) * mm, "end": v(5.22, -20.4) * mm});
            skLineSegment(sketch, "E145.0.1.96", {"start": v(-22.63, -28.68) * mm, "end": v(-26.5, -27.64) * mm});
            skLineSegment(sketch, "E145.0.1.97", {"start": v(14.06, -21.49) * mm, "end": v(11.14, -24.22) * mm});
            skLineSegment(sketch, "E145.0.1.98", {"start": v(23.46, -36.29) * mm, "end": v(23.43, -36.79) * mm});
            skLineSegment(sketch, "E145.0.1.99", {"start": v(-11.53, -55.47) * mm, "end": v(-13.53, -58.94) * mm});
            skLineSegment(sketch, "E145.0.1.100", {"start": v(2.93, -15.72) * mm, "end": v(3.42, -15.8) * mm});
            skLineSegment(sketch, "E145.0.1.101", {"start": v(9.24, -22.55) * mm, "end": v(9.63, -22.86) * mm});
            skLineSegment(sketch, "E145.0.1.102", {"start": v(17.83, -50.3) * mm, "end": v(17.5, -50.68) * mm});
            skLineSegment(sketch, "E145.0.1.103", {"start": v(2.93, -15.72) * mm, "end": v(2.28, -19.67) * mm});
            skLineSegment(sketch, "E145.0.1.104", {"start": v(14.5, -48.04) * mm, "end": v(11.49, -45.4) * mm});
            skLineSegment(sketch, "E145.0.1.105", {"start": v(3.42, -15.8) * mm, "end": v(2.77, -19.75) * mm});
            skLineSegment(sketch, "E145.0.1.106", {"start": v(17.66, -26.73) * mm, "end": v(14.01, -28.38) * mm});
            skLineSegment(sketch, "E145.0.1.107", {"start": v(13.3, -42.97) * mm, "end": v(13.03, -43.4) * mm});
            skLineSegment(sketch, "E145.0.1.108", {"start": v(12.07, -19.68) * mm, "end": v(9.63, -22.86) * mm});
            skLineSegment(sketch, "E145.0.1.109", {"start": v(16.69, -45.08) * mm, "end": v(13.3, -42.97) * mm});
            skLineSegment(sketch, "E145.0.1.110", {"start": v(7.09, -21.21) * mm, "end": v(7.53, -21.45) * mm});
            skLineSegment(sketch, "E145.0.1.111", {"start": v(7.32, -12.67) * mm, "end": v(7.79, -12.83) * mm});
            skLineSegment(sketch, "E145.0.1.112", {"start": v(-11.97, -55.22) * mm, "end": v(-13.97, -58.69) * mm});
            skLineSegment(sketch, "E145.0.1.113", {"start": v(6.03, -16.46) * mm, "end": v(4.74, -20.24) * mm});
            skLineSegment(sketch, "E145.0.1.114", {"start": v(12.56, -49.91) * mm, "end": v(12.18, -50.23) * mm});
            skLineSegment(sketch, "E145.0.1.115", {"start": v(16.35, -24.38) * mm, "end": v(13.02, -26.6) * mm});
            skLineSegment(sketch, "E145.0.1.116", {"start": v(4.74, -20.24) * mm, "end": v(5.22, -20.4) * mm});
            skLineSegment(sketch, "E145.0.1.117", {"start": v(19.4, -21.74) * mm, "end": v(19.68, -22.15) * mm});
            skLineSegment(sketch, "E145.0.1.118", {"start": v(19.38, -32.84) * mm, "end": v(15.4, -33.23) * mm});
            skLineSegment(sketch, "E145.0.1.119", {"start": v(-22.76, -29.16) * mm, "end": v(-26.63, -28.12) * mm});
            skLineSegment(sketch, "E145.0.1.120", {"start": v(15.4, -33.23) * mm, "end": v(15.45, -33.73) * mm});
            skLineSegment(sketch, "E145.0.1.121", {"start": v(8.97, -17.69) * mm, "end": v(9.41, -17.92) * mm});
            skLineSegment(sketch, "E145.0.1.122", {"start": v(12.75, -26.18) * mm, "end": v(13.02, -26.6) * mm});
            skLineSegment(sketch, "E145.0.1.123", {"start": v(-26.5, -27.64) * mm, "end": v(-26.63, -28.12) * mm});
            skLineSegment(sketch, "E145.0.1.124", {"start": v(-13.97, -58.69) * mm, "end": v(-13.53, -58.94) * mm});
            skLineSegment(sketch, "E145.0.1.125", {"start": v(11.14, -24.22) * mm, "end": v(11.48, -24.59) * mm});
            skLineSegment(sketch, "E145.0.1.126", {"start": v(-11.97, -55.22) * mm, "end": v(-13.97, -58.69) * mm});
            skLineSegment(sketch, "E145.0.1.127", {"start": v(11.82, -45.03) * mm, "end": v(11.49, -45.4) * mm});
            skLineSegment(sketch, "E145.0.1.128", {"start": v(2.28, -19.67) * mm, "end": v(2.77, -19.75) * mm});
            skLineSegment(sketch, "E145.0.1.129", {"start": v(18.77, -29.71) * mm, "end": v(14.9, -30.75) * mm});
            skLineSegment(sketch, "E145.0.1.130", {"start": v(12.18, -50.23) * mm, "end": v(9.64, -47.14) * mm});
            skLineSegment(sketch, "E145.0.1.131", {"start": v(15.15, -38.28) * mm, "end": v(15.04, -38.76) * mm});
            skLineSegment(sketch, "E145.0.1.132", {"start": v(18.9, -30.2) * mm, "end": v(15.03, -31.23) * mm});
            skLineSegment(sketch, "E145.0.1.133", {"start": v(19.05, -39.18) * mm, "end": v(18.93, -39.67) * mm});
            skLineSegment(sketch, "E145.0.1.134", {"start": v(-11.53, -55.47) * mm, "end": v(-13.53, -58.94) * mm});
            skLineSegment(sketch, "E145.0.1.135", {"start": v(18.93, -39.67) * mm, "end": v(15.04, -38.76) * mm});
            skLineSegment(sketch, "E145.0.1.136", {"start": v(14.01, -28.38) * mm, "end": v(14.22, -28.83) * mm});
            skLineSegment(sketch, "E145.0.1.137", {"start": v(-22.76, -29.16) * mm, "end": v(-26.63, -28.12) * mm});
            skLineSegment(sketch, "E145.0.1.138", {"start": v(2.93, -15.72) * mm, "end": v(3.42, -15.8) * mm});
            skLineSegment(sketch, "E145.0.1.139", {"start": v(-22.63, -28.68) * mm, "end": v(-26.5, -27.64) * mm});
            skLineSegment(sketch, "E145.0.1.140", {"start": v(-0.25, -11.5) * mm, "end": v(0.25, -11.5) * mm});
            skLineSegment(sketch, "E145.0.1.141", {"start": v(0.25, -15.5) * mm, "end": v(0.25, -11.5) * mm});
            skLineSegment(sketch, "E145.0.1.142", {"start": v(-0.25, -15.5) * mm, "end": v(-0.25, -11.5) * mm});
            skLineSegment(sketch, "E145.0.1.143", {"start": v(17.86, -27.18) * mm, "end": v(14.22, -28.83) * mm});
            skLineSegment(sketch, "E145.0.1.144", {"start": v(19.4, -21.74) * mm, "end": v(19.68, -22.15) * mm});
            skLineSegment(sketch, "E145.0.1.145", {"start": v(19.43, -33.34) * mm, "end": v(15.45, -33.73) * mm});
            skLineSegment(sketch, "E145.0.1.146", {"start": v(12.56, -49.91) * mm, "end": v(10.03, -46.82) * mm});
            skLineSegment(sketch, "E145.0.1.147", {"start": v(12.56, -49.91) * mm, "end": v(12.18, -50.23) * mm});
            skLineSegment(sketch, "E145.0.1.148", {"start": v(14.9, -30.75) * mm, "end": v(15.03, -31.23) * mm});
            skLineSegment(sketch, "E145.0.1.149", {"start": v(-26.5, -27.64) * mm, "end": v(-26.63, -28.12) * mm});
            skLineSegment(sketch, "E145.0.1.150", {"start": v(10.03, -46.82) * mm, "end": v(9.64, -47.14) * mm});
            skLineSegment(sketch, "E145.0.1.151", {"start": v(8.97, -17.69) * mm, "end": v(9.41, -17.92) * mm});
            skLineSegment(sketch, "E145.0.1.152", {"start": v(19.38, -32.84) * mm, "end": v(19.43, -33.34) * mm});
            skLineSegment(sketch, "E145.0.1.153", {"start": v(16.69, -45.08) * mm, "end": v(16.43, -45.5) * mm});
            skLineSegment(sketch, "E145.0.1.154", {"start": v(12.07, -19.68) * mm, "end": v(14.5, -16.5) * mm});
            skLineSegment(sketch, "E145.0.1.155", {"start": v(-16.69, -45.08) * mm, "end": v(-13.3, -42.97) * mm});
            skLineSegment(sketch, "E145.0.1.156", {"start": v(-13.3, -42.97) * mm, "end": v(-13.03, -43.4) * mm});
            skLineSegment(sketch, "E145.0.1.157", {"start": v(-14.5, -48.04) * mm, "end": v(-17.5, -50.68) * mm});
            skLineSegment(sketch, "E145.0.1.158", {"start": v(-6.5, -16.62) * mm, "end": v(-5.22, -20.4) * mm});
            skLineSegment(sketch, "E145.0.1.159", {"start": v(18.77, -29.71) * mm, "end": v(18.9, -30.2) * mm});
            skLineSegment(sketch, "E145.0.1.160", {"start": v(18.77, -29.71) * mm, "end": v(22.63, -28.68) * mm});
            skLineSegment(sketch, "E145.0.1.161", {"start": v(17.66, -26.73) * mm, "end": v(17.86, -27.18) * mm});
            skLineSegment(sketch, "E145.0.1.162", {"start": v(15.48, -35.76) * mm, "end": v(15.45, -36.26) * mm});
            skLineSegment(sketch, "E145.0.1.163", {"start": v(7.97, -48.3) * mm, "end": v(7.53, -48.55) * mm});
            skLineSegment(sketch, "E145.0.1.164", {"start": v(18.9, -30.2) * mm, "end": v(22.76, -29.16) * mm});
            skLineSegment(sketch, "E145.0.1.165", {"start": v(-13.97, -58.69) * mm, "end": v(-13.53, -58.94) * mm});
            skLineSegment(sketch, "E145.0.1.166", {"start": v(18.1, -42.23) * mm, "end": v(21.8, -43.76) * mm});
            skLineSegment(sketch, "E145.0.1.167", {"start": v(-0.25, -11.5) * mm, "end": v(0.25, -11.5) * mm});
            skLineSegment(sketch, "E145.0.1.168", {"start": v(19.47, -36.03) * mm, "end": v(15.48, -35.76) * mm});
            skLineSegment(sketch, "E145.0.1.169", {"start": v(9.97, -51.76) * mm, "end": v(7.97, -48.3) * mm});
            skLineSegment(sketch, "E145.0.1.170", {"start": v(16.69, -45.08) * mm, "end": v(16.43, -45.5) * mm});
            skLineSegment(sketch, "E145.0.1.171", {"start": v(-18.1, -42.23) * mm, "end": v(-14.41, -40.7) * mm});
            skLineSegment(sketch, "E145.0.1.172", {"start": v(14.82, -47.67) * mm, "end": v(14.5, -48.04) * mm});
            skLineSegment(sketch, "E145.0.1.173", {"start": v(14.06, -21.49) * mm, "end": v(14.4, -21.85) * mm});
            skLineSegment(sketch, "E145.0.1.174", {"start": v(-14.4, -21.85) * mm, "end": v(-11.48, -24.59) * mm});
            skLineSegment(sketch, "E145.0.1.175", {"start": v(19.38, -32.84) * mm, "end": v(19.43, -33.34) * mm});
            skLineSegment(sketch, "E145.0.1.176", {"start": v(-14.82, -47.67) * mm, "end": v(-17.83, -50.3) * mm});
            skLineSegment(sketch, "E145.0.1.177", {"start": v(-18.77, -29.71) * mm, "end": v(-14.9, -30.75) * mm});
            skLineSegment(sketch, "E145.0.1.178", {"start": v(-19.47, -36.03) * mm, "end": v(-23.46, -36.29) * mm});
            skLineSegment(sketch, "E145.0.1.179", {"start": v(-17.92, -42.7) * mm, "end": v(-14.22, -41.16) * mm});
            skLineSegment(sketch, "E145.0.1.180", {"start": v(-16.43, -45.5) * mm, "end": v(-13.03, -43.4) * mm});
            skLineSegment(sketch, "E145.0.1.181", {"start": v(14.1, -16.2) * mm, "end": v(14.5, -16.5) * mm});
            skLineSegment(sketch, "E145.0.1.182", {"start": v(-16.69, -45.08) * mm, "end": v(-16.43, -45.5) * mm});
            skLineSegment(sketch, "E145.0.1.183", {"start": v(21.8, -43.76) * mm, "end": v(21.61, -44.22) * mm});
            skLineSegment(sketch, "E145.0.1.184", {"start": v(16.07, -23.96) * mm, "end": v(16.35, -24.38) * mm});
            skLineSegment(sketch, "E145.0.1.185", {"start": v(17.92, -42.7) * mm, "end": v(21.61, -44.22) * mm});
            skLineSegment(sketch, "E145.0.1.186", {"start": v(9.53, -52.01) * mm, "end": v(7.53, -48.55) * mm});
            skLineSegment(sketch, "E145.0.1.187", {"start": v(19.44, -36.52) * mm, "end": v(15.45, -36.26) * mm});
            skLineSegment(sketch, "E145.0.1.188", {"start": v(-6.03, -16.46) * mm, "end": v(-4.74, -20.24) * mm});
            skLineSegment(sketch, "E145.0.1.189", {"start": v(-23.46, -36.29) * mm, "end": v(-23.43, -36.79) * mm});
            skLineSegment(sketch, "E145.0.1.190", {"start": v(-16.35, -24.38) * mm, "end": v(-13.02, -26.6) * mm});
            skLineSegment(sketch, "E145.0.1.191", {"start": v(-8.97, -17.69) * mm, "end": v(-9.41, -17.92) * mm});
            skLineSegment(sketch, "E145.0.1.192", {"start": v(-17.83, -50.3) * mm, "end": v(-17.5, -50.68) * mm});
            skLineSegment(sketch, "E145.0.1.193", {"start": v(-14.82, -47.67) * mm, "end": v(-11.82, -45.03) * mm});
            skLineSegment(sketch, "E145.0.1.194", {"start": v(-19.44, -36.52) * mm, "end": v(-23.43, -36.79) * mm});
            skLineSegment(sketch, "E145.0.1.195", {"start": v(11.67, -19.38) * mm, "end": v(14.1, -16.2) * mm});
            skLineSegment(sketch, "E145.0.1.196", {"start": v(-8.97, -17.69) * mm, "end": v(-7.09, -21.21) * mm});
            skLineSegment(sketch, "E145.0.1.197", {"start": v(-9.41, -17.92) * mm, "end": v(-7.53, -21.45) * mm});
            skLineSegment(sketch, "E145.0.1.198", {"start": v(-16.07, -23.96) * mm, "end": v(-12.75, -26.18) * mm});
            skLineSegment(sketch, "E145.0.1.199", {"start": v(-8.97, -17.69) * mm, "end": v(-7.09, -21.21) * mm});
            skLineSegment(sketch, "E145.0.1.200", {"start": v(18.77, -29.71) * mm, "end": v(18.9, -30.2) * mm});
            skLineSegment(sketch, "E145.0.1.201", {"start": v(-6.5, -16.62) * mm, "end": v(-7.79, -12.83) * mm});
            skLineSegment(sketch, "E145.0.1.202", {"start": v(-9.41, -17.92) * mm, "end": v(-7.53, -21.45) * mm});
            skLineSegment(sketch, "E145.0.1.203", {"start": v(14.82, -47.67) * mm, "end": v(14.5, -48.04) * mm});
            skLineSegment(sketch, "E145.0.1.204", {"start": v(-6.5, -16.62) * mm, "end": v(-5.22, -20.4) * mm});
            skLineSegment(sketch, "E145.0.1.205", {"start": v(14.06, -21.49) * mm, "end": v(14.4, -21.85) * mm});
            skLineSegment(sketch, "E145.0.1.206", {"start": v(-7.09, -21.21) * mm, "end": v(-7.53, -21.45) * mm});
            skLineSegment(sketch, "E145.0.1.207", {"start": v(-14.5, -48.04) * mm, "end": v(-11.49, -45.4) * mm});
            skLineSegment(sketch, "E145.0.1.208", {"start": v(-16.07, -23.96) * mm, "end": v(-12.75, -26.18) * mm});
            skLineSegment(sketch, "E145.0.1.209", {"start": v(-19.44, -36.52) * mm, "end": v(-23.43, -36.79) * mm});
            skLineSegment(sketch, "E145.0.1.210", {"start": v(-13.3, -42.97) * mm, "end": v(-13.03, -43.4) * mm});
            skLineSegment(sketch, "E145.0.1.211", {"start": v(-14.82, -47.67) * mm, "end": v(-11.82, -45.03) * mm});
            skLineSegment(sketch, "E145.0.1.212", {"start": v(-14.4, -21.85) * mm, "end": v(-11.48, -24.59) * mm});
            skLineSegment(sketch, "E145.0.1.213", {"start": v(17.66, -26.73) * mm, "end": v(17.86, -27.18) * mm});
            skLineSegment(sketch, "E145.0.1.214", {"start": v(-0.25, -15.5) * mm, "end": v(-0.25, -19.5) * mm});
            skLineSegment(sketch, "E145.0.1.215", {"start": v(0.25, -15.5) * mm, "end": v(0.25, -19.5) * mm});
            skLineSegment(sketch, "E145.0.1.216", {"start": v(-0.25, -15.5) * mm, "end": v(0.25, -15.5) * mm});
            skLineSegment(sketch, "E145.0.1.217", {"start": v(-0.25, -19.5) * mm, "end": v(0.25, -19.5) * mm});
            skLineSegment(sketch, "E145.0.1.218", {"start": v(-14.5, -48.04) * mm, "end": v(-17.5, -50.68) * mm});
            skLineSegment(sketch, "E145.0.1.219", {"start": v(-16.69, -45.08) * mm, "end": v(-13.3, -42.97) * mm});
            skLineSegment(sketch, "E145.0.1.220", {"start": v(-18.1, -42.23) * mm, "end": v(-14.41, -40.7) * mm});
            skLineSegment(sketch, "E145.0.1.221", {"start": v(-17.92, -42.7) * mm, "end": v(-14.22, -41.16) * mm});
            skLineSegment(sketch, "E145.0.1.222", {"start": v(-7.32, -12.67) * mm, "end": v(-7.79, -12.83) * mm});
            skLineSegment(sketch, "E145.0.1.223", {"start": v(14.1, -16.2) * mm, "end": v(14.5, -16.5) * mm});
            skLineSegment(sketch, "E145.0.1.224", {"start": v(21.8, -43.76) * mm, "end": v(21.61, -44.22) * mm});
            skLineSegment(sketch, "E145.0.1.225", {"start": v(-14.9, -30.75) * mm, "end": v(-15.03, -31.23) * mm});
            skLineSegment(sketch, "E145.0.1.226", {"start": v(-6.03, -16.46) * mm, "end": v(-7.32, -12.67) * mm});
            skLineSegment(sketch, "E145.0.1.227", {"start": v(-14.82, -47.67) * mm, "end": v(-17.83, -50.3) * mm});
            skLineSegment(sketch, "E145.0.1.228", {"start": v(-12.56, -49.91) * mm, "end": v(-10.03, -46.82) * mm});
            skLineSegment(sketch, "E145.0.1.229", {"start": v(-16.69, -45.08) * mm, "end": v(-16.43, -45.5) * mm});
            skLineSegment(sketch, "E145.0.1.230", {"start": v(9.53, -52.01) * mm, "end": v(11.53, -55.47) * mm});
            skLineSegment(sketch, "E145.0.1.231", {"start": v(-4.74, -20.24) * mm, "end": v(-5.22, -20.4) * mm});
            skLineSegment(sketch, "E145.0.1.232", {"start": v(18.1, -42.23) * mm, "end": v(17.92, -42.7) * mm});
            skLineSegment(sketch, "E145.0.1.233", {"start": v(-14.06, -21.49) * mm, "end": v(-11.14, -24.22) * mm});
            skLineSegment(sketch, "E145.0.1.234", {"start": v(9.97, -51.76) * mm, "end": v(11.97, -55.22) * mm});
            skLineSegment(sketch, "E145.0.1.235", {"start": v(16.07, -23.96) * mm, "end": v(16.35, -24.38) * mm});
            skLineSegment(sketch, "E145.0.1.236", {"start": v(-17.83, -50.3) * mm, "end": v(-17.5, -50.68) * mm});
            skLineSegment(sketch, "E145.0.1.237", {"start": v(-16.35, -24.38) * mm, "end": v(-13.02, -26.6) * mm});
            skLineSegment(sketch, "E145.0.1.238", {"start": v(9.97, -51.76) * mm, "end": v(9.53, -52.01) * mm});
            skLineSegment(sketch, "E145.0.1.239", {"start": v(-14.01, -28.38) * mm, "end": v(-14.22, -28.83) * mm});
            skLineSegment(sketch, "E145.0.1.240", {"start": v(-11.82, -45.03) * mm, "end": v(-11.49, -45.4) * mm});
            skLineSegment(sketch, "E145.0.1.241", {"start": v(11.97, -55.22) * mm, "end": v(11.53, -55.47) * mm});
            skLineSegment(sketch, "E145.0.1.242", {"start": v(-14.06, -21.49) * mm, "end": v(-14.4, -21.85) * mm});
            skLineSegment(sketch, "E145.0.1.243", {"start": v(-17.66, -26.73) * mm, "end": v(-14.01, -28.38) * mm});
            skLineSegment(sketch, "E145.0.1.244", {"start": v(-18.77, -29.71) * mm, "end": v(-14.9, -30.75) * mm});
            skLineSegment(sketch, "E145.0.1.245", {"start": v(-16.43, -45.5) * mm, "end": v(-13.03, -43.4) * mm});
            skLineSegment(sketch, "E145.0.1.246", {"start": v(-19.47, -36.03) * mm, "end": v(-23.46, -36.29) * mm});
            skLineSegment(sketch, "E145.0.1.247", {"start": v(-8.97, -17.69) * mm, "end": v(-9.41, -17.92) * mm});
            skLineSegment(sketch, "E145.0.1.248", {"start": v(-14.41, -40.7) * mm, "end": v(-14.22, -41.16) * mm});
            skLineSegment(sketch, "E145.0.1.249", {"start": v(-8.97, -17.69) * mm, "end": v(-9.41, -17.92) * mm});
            skLineSegment(sketch, "E145.0.1.250", {"start": v(-16.69, -45.08) * mm, "end": v(-16.43, -45.5) * mm});
            skLineSegment(sketch, "E145.0.1.251", {"start": v(14.82, -47.67) * mm, "end": v(14.5, -48.04) * mm});
            skLineSegment(sketch, "E145.0.1.252", {"start": v(-14.9, -30.75) * mm, "end": v(-15.03, -31.23) * mm});
            skLineSegment(sketch, "E145.0.1.253", {"start": v(14.1, -16.2) * mm, "end": v(14.5, -16.5) * mm});
            skLineSegment(sketch, "E145.0.1.254", {"start": v(-14.1, -16.2) * mm, "end": v(-16.54, -13.03) * mm});
            skLineSegment(sketch, "E145.0.1.255", {"start": v(18.77, -29.71) * mm, "end": v(18.9, -30.2) * mm});
            skLineSegment(sketch, "E145.0.1.256", {"start": v(-14.41, -40.7) * mm, "end": v(-14.22, -41.16) * mm});
            skLineSegment(sketch, "E145.0.1.257", {"start": v(-12.07, -19.68) * mm, "end": v(-9.63, -22.86) * mm});
            skLineSegment(sketch, "E145.0.1.258", {"start": v(-17.86, -27.18) * mm, "end": v(-14.22, -28.83) * mm});
            skLineSegment(sketch, "E145.0.1.259", {"start": v(21.8, -43.76) * mm, "end": v(21.61, -44.22) * mm});
            skLineSegment(sketch, "E145.0.1.260", {"start": v(-18.9, -30.2) * mm, "end": v(-15.03, -31.23) * mm});
            skLineSegment(sketch, "E145.0.1.261", {"start": v(-7.09, -21.21) * mm, "end": v(-7.53, -21.45) * mm});
            skLineSegment(sketch, "E145.0.1.262", {"start": v(-6.03, -16.46) * mm, "end": v(-7.32, -12.67) * mm});
            skLineSegment(sketch, "E145.0.1.263", {"start": v(-17.66, -26.73) * mm, "end": v(-14.01, -28.38) * mm});
            skLineSegment(sketch, "E145.0.1.264", {"start": v(-19.38, -32.84) * mm, "end": v(-15.4, -33.23) * mm});
            skLineSegment(sketch, "E145.0.1.265", {"start": v(-9.53, -52.01) * mm, "end": v(-7.53, -48.55) * mm});
            skLineSegment(sketch, "E145.0.1.266", {"start": v(-17.83, -50.3) * mm, "end": v(-17.5, -50.68) * mm});
            skLineSegment(sketch, "E145.0.1.267", {"start": v(-6.03, -16.46) * mm, "end": v(-4.74, -20.24) * mm});
            skLineSegment(sketch, "E145.0.1.268", {"start": v(-12.56, -49.91) * mm, "end": v(-10.03, -46.82) * mm});
            skLineSegment(sketch, "E145.0.1.269", {"start": v(-12.18, -50.23) * mm, "end": v(-9.64, -47.14) * mm});
            skLineSegment(sketch, "E145.0.1.270", {"start": v(-6.5, -16.62) * mm, "end": v(-7.79, -12.83) * mm});
            skLineSegment(sketch, "E145.0.1.271", {"start": v(-14.5, -48.04) * mm, "end": v(-11.49, -45.4) * mm});
            skLineSegment(sketch, "E145.0.1.272", {"start": v(-0.25, -15.5) * mm, "end": v(0.25, -15.5) * mm});
            skLineSegment(sketch, "E145.0.1.273", {"start": v(-4.74, -20.24) * mm, "end": v(-5.22, -20.4) * mm});
            skLineSegment(sketch, "E145.0.1.274", {"start": v(18.1, -42.23) * mm, "end": v(17.92, -42.7) * mm});
            skLineSegment(sketch, "E145.0.1.275", {"start": v(-23.46, -36.29) * mm, "end": v(-23.43, -36.79) * mm});
            skLineSegment(sketch, "E145.0.1.276", {"start": v(-12.75, -26.18) * mm, "end": v(-13.02, -26.6) * mm});
            skLineSegment(sketch, "E145.0.1.277", {"start": v(-11.82, -45.03) * mm, "end": v(-11.49, -45.4) * mm});
            skLineSegment(sketch, "E145.0.1.278", {"start": v(-14.01, -28.38) * mm, "end": v(-14.22, -28.83) * mm});
            skLineSegment(sketch, "E145.0.1.279", {"start": v(-3.42, -15.8) * mm, "end": v(-2.77, -19.75) * mm});
            skLineSegment(sketch, "E145.0.1.280", {"start": v(-10.03, -46.82) * mm, "end": v(-9.64, -47.14) * mm});
            skLineSegment(sketch, "E145.0.1.281", {"start": v(9.97, -51.76) * mm, "end": v(9.53, -52.01) * mm});
            skLineSegment(sketch, "E145.0.1.282", {"start": v(-14.06, -21.49) * mm, "end": v(-14.4, -21.85) * mm});
            skLineSegment(sketch, "E145.0.1.283", {"start": v(16.07, -23.96) * mm, "end": v(16.35, -24.38) * mm});
            skLineSegment(sketch, "E145.0.1.284", {"start": v(-15.4, -33.23) * mm, "end": v(-15.45, -33.73) * mm});
            skLineSegment(sketch, "E145.0.1.285", {"start": v(-16.54, -13.03) * mm, "end": v(-16.94, -13.34) * mm});
            skLineSegment(sketch, "E145.0.1.286", {"start": v(-7.97, -48.3) * mm, "end": v(-7.53, -48.55) * mm});
            skLineSegment(sketch, "E145.0.1.287", {"start": v(11.97, -55.22) * mm, "end": v(11.53, -55.47) * mm});
            skLineSegment(sketch, "E145.0.1.288", {"start": v(-25.5, -45.3) * mm, "end": v(-25.3, -45.75) * mm});
            skLineSegment(sketch, "E145.0.1.289", {"start": v(-11.67, -19.38) * mm, "end": v(-9.24, -22.55) * mm});
            skLineSegment(sketch, "E145.0.1.290", {"start": v(-2.93, -15.72) * mm, "end": v(-2.28, -19.67) * mm});
            skLineSegment(sketch, "E145.0.1.291", {"start": v(-21.8, -43.76) * mm, "end": v(-25.5, -45.3) * mm});
            skLineSegment(sketch, "E145.0.1.292", {"start": v(-7.32, -12.67) * mm, "end": v(-7.79, -12.83) * mm});
            skLineSegment(sketch, "E145.0.1.293", {"start": v(-9.97, -51.76) * mm, "end": v(-7.97, -48.3) * mm});
            skLineSegment(sketch, "E145.0.1.294", {"start": v(-21.61, -44.22) * mm, "end": v(-25.3, -45.75) * mm});
            skLineSegment(sketch, "E145.0.1.295", {"start": v(-14.06, -21.49) * mm, "end": v(-11.14, -24.22) * mm});
            skLineSegment(sketch, "E145.0.1.296", {"start": v(-9.24, -22.55) * mm, "end": v(-9.63, -22.86) * mm});
            skLineSegment(sketch, "E145.0.1.297", {"start": v(-2.93, -15.72) * mm, "end": v(-2.28, -19.67) * mm});
            skLineSegment(sketch, "E145.0.1.298", {"start": v(-21.61, -44.22) * mm, "end": v(-25.3, -45.75) * mm});
            skLineSegment(sketch, "E145.0.1.299", {"start": v(-12.75, -26.18) * mm, "end": v(-13.02, -26.6) * mm});
            skLineSegment(sketch, "E145.0.1.300", {"start": v(-9.97, -51.76) * mm, "end": v(-7.97, -48.3) * mm});
            skLineSegment(sketch, "E145.0.1.301", {"start": v(18.77, -29.71) * mm, "end": v(18.9, -30.2) * mm});
            skLineSegment(sketch, "E145.0.1.302", {"start": v(-7.32, -12.67) * mm, "end": v(-7.79, -12.83) * mm});
            skLineSegment(sketch, "E145.0.1.303", {"start": v(14.82, -47.67) * mm, "end": v(14.5, -48.04) * mm});
            skLineSegment(sketch, "E145.0.1.304", {"start": v(-14.1, -16.2) * mm, "end": v(-16.54, -13.03) * mm});
            skLineSegment(sketch, "E145.0.1.305", {"start": v(-11.14, -24.22) * mm, "end": v(-11.48, -24.59) * mm});
            skLineSegment(sketch, "E145.0.1.306", {"start": v(-19.38, -32.84) * mm, "end": v(-15.4, -33.23) * mm});
            skLineSegment(sketch, "E145.0.1.307", {"start": v(18.1, -42.23) * mm, "end": v(17.92, -42.7) * mm});
            skLineSegment(sketch, "E145.0.1.308", {"start": v(-12.07, -19.68) * mm, "end": v(-9.63, -22.86) * mm});
            skLineSegment(sketch, "E145.0.1.309", {"start": v(-9.53, -52.01) * mm, "end": v(-7.53, -48.55) * mm});
            skLineSegment(sketch, "E145.0.1.310", {"start": v(21.8, -43.76) * mm, "end": v(21.61, -44.22) * mm});
            skLineSegment(sketch, "E145.0.1.311", {"start": v(-14.5, -16.5) * mm, "end": v(-16.94, -13.34) * mm});
            skLineSegment(sketch, "E145.0.1.312", {"start": v(-21.8, -43.76) * mm, "end": v(-25.5, -45.3) * mm});
            skLineSegment(sketch, "E145.0.1.313", {"start": v(-16.69, -45.08) * mm, "end": v(-16.43, -45.5) * mm});
            skLineSegment(sketch, "E145.0.1.314", {"start": v(-17.83, -50.3) * mm, "end": v(-17.5, -50.68) * mm});
            skLineSegment(sketch, "E145.0.1.315", {"start": v(9.97, -51.76) * mm, "end": v(9.53, -52.01) * mm});
            skLineSegment(sketch, "E145.0.1.316", {"start": v(-18.9, -30.2) * mm, "end": v(-15.03, -31.23) * mm});
            skLineSegment(sketch, "E145.0.1.317", {"start": v(-12.18, -50.23) * mm, "end": v(-9.64, -47.14) * mm});
            skLineSegment(sketch, "E145.0.1.318", {"start": v(16.07, -23.96) * mm, "end": v(16.35, -24.38) * mm});
            skLineSegment(sketch, "E145.0.1.319", {"start": v(-8.97, -17.69) * mm, "end": v(-9.41, -17.92) * mm});
            skLineSegment(sketch, "E145.0.1.320", {"start": v(14.1, -16.2) * mm, "end": v(14.5, -16.5) * mm});
            skLineSegment(sketch, "E145.0.1.321", {"start": v(-16.54, -13.03) * mm, "end": v(-16.94, -13.34) * mm});
            skLineSegment(sketch, "E145.0.1.322", {"start": v(-17.86, -27.18) * mm, "end": v(-14.22, -28.83) * mm});
            skLineSegment(sketch, "E145.0.1.323", {"start": v(-14.06, -21.49) * mm, "end": v(-14.4, -21.85) * mm});
            skLineSegment(sketch, "E145.0.1.324", {"start": v(11.97, -55.22) * mm, "end": v(11.53, -55.47) * mm});
            skLineSegment(sketch, "E145.0.1.325", {"start": v(-11.67, -19.38) * mm, "end": v(-9.24, -22.55) * mm});
            skLineSegment(sketch, "E145.0.1.326", {"start": v(-23.46, -36.29) * mm, "end": v(-23.43, -36.79) * mm});
            skLineSegment(sketch, "E145.0.1.327", {"start": v(-9.24, -22.55) * mm, "end": v(-9.63, -22.86) * mm});
            skLineSegment(sketch, "E145.0.1.328", {"start": v(-3.42, -15.8) * mm, "end": v(-2.77, -19.75) * mm});
            skLineSegment(sketch, "E145.0.1.329", {"start": v(-10.03, -46.82) * mm, "end": v(-9.64, -47.14) * mm});
            skLineSegment(sketch, "E145.0.1.330", {"start": v(-15.4, -33.23) * mm, "end": v(-15.45, -33.73) * mm});
            skLineSegment(sketch, "E145.0.1.331", {"start": v(-23.46, -36.29) * mm, "end": v(-23.43, -36.79) * mm});
            skLineSegment(sketch, "E145.0.1.332", {"start": v(-14.06, -21.49) * mm, "end": v(-14.4, -21.85) * mm});
            skLineSegment(sketch, "E145.0.1.333", {"start": v(-2.28, -19.67) * mm, "end": v(-2.77, -19.75) * mm});
            skLineSegment(sketch, "E145.0.1.334", {"start": v(-15.48, -35.76) * mm, "end": v(-15.45, -36.26) * mm});
            skLineSegment(sketch, "E145.0.1.335", {"start": v(-7.32, -12.67) * mm, "end": v(-7.79, -12.83) * mm});
            skLineSegment(sketch, "E145.0.1.336", {"start": v(-19.43, -33.34) * mm, "end": v(-15.45, -33.73) * mm});
            skLineSegment(sketch, "E145.0.1.337", {"start": v(-25.5, -45.3) * mm, "end": v(-25.3, -45.75) * mm});
            skLineSegment(sketch, "E145.0.1.338", {"start": v(-7.97, -48.3) * mm, "end": v(-7.53, -48.55) * mm});
            skLineSegment(sketch, "E145.0.1.339", {"start": v(-14.5, -16.5) * mm, "end": v(-16.94, -13.34) * mm});
            skLineSegment(sketch, "E145.0.1.340", {"start": v(-11.14, -24.22) * mm, "end": v(-11.48, -24.59) * mm});
            skLineSegment(sketch, "E145.0.1.341", {"start": v(9.97, -51.76) * mm, "end": v(9.53, -52.01) * mm});
            skLineSegment(sketch, "E145.0.1.342", {"start": v(18.1, -42.23) * mm, "end": v(17.92, -42.7) * mm});
            skLineSegment(sketch, "E145.0.1.343", {"start": v(-19.38, -32.84) * mm, "end": v(-19.43, -33.34) * mm});
            skLineSegment(sketch, "E145.0.1.344", {"start": v(-19.05, -39.18) * mm, "end": v(-15.15, -38.28) * mm});
            skLineSegment(sketch, "E145.0.1.345", {"start": v(-19.47, -36.03) * mm, "end": v(-15.48, -35.76) * mm});
            skLineSegment(sketch, "E145.0.1.346", {"start": v(-18.93, -39.67) * mm, "end": v(-15.04, -38.76) * mm});
            skLineSegment(sketch, "E145.0.1.347", {"start": v(-19.44, -36.52) * mm, "end": v(-15.45, -36.26) * mm});
            skLineSegment(sketch, "E145.0.1.348", {"start": v(11.97, -55.22) * mm, "end": v(11.53, -55.47) * mm});
            skLineSegment(sketch, "E145.0.1.349", {"start": v(-2.28, -19.67) * mm, "end": v(-2.77, -19.75) * mm});
            skLineSegment(sketch, "E145.0.1.350", {"start": v(-19.43, -33.34) * mm, "end": v(-15.45, -33.73) * mm});
            skLineSegment(sketch, "E145.0.1.351", {"start": v(-19.47, -36.03) * mm, "end": v(-15.48, -35.76) * mm});
            skLineSegment(sketch, "E145.0.1.352", {"start": v(-15.48, -35.76) * mm, "end": v(-15.45, -36.26) * mm});
            skLineSegment(sketch, "E145.0.1.353", {"start": v(-19.05, -39.18) * mm, "end": v(-15.15, -38.28) * mm});
            skLineSegment(sketch, "E145.0.1.354", {"start": v(-18.93, -39.67) * mm, "end": v(-15.04, -38.76) * mm});
            skLineSegment(sketch, "E145.0.1.355", {"start": v(-19.38, -32.84) * mm, "end": v(-19.43, -33.34) * mm});
            skLineSegment(sketch, "E145.0.1.356", {"start": v(-19.44, -36.52) * mm, "end": v(-15.45, -36.26) * mm});
            skLineSegment(sketch, "E145.0.1.357", {"start": v(-18.1, -42.23) * mm, "end": v(-21.8, -43.76) * mm});
            skLineSegment(sketch, "E145.0.1.358", {"start": v(-19.05, -39.18) * mm, "end": v(-18.93, -39.67) * mm});
            skLineSegment(sketch, "E145.0.1.359", {"start": v(22.63, -28.68) * mm, "end": v(22.76, -29.16) * mm});
            skLineSegment(sketch, "E145.0.1.360", {"start": v(6.03, -16.46) * mm, "end": v(6.5, -16.62) * mm});
            skLineSegment(sketch, "E145.0.1.361", {"start": v(-12.07, -19.68) * mm, "end": v(-14.5, -16.5) * mm});
            skLineSegment(sketch, "E145.0.1.362", {"start": v(-16.35, -24.38) * mm, "end": v(-19.68, -22.15) * mm});
            skLineSegment(sketch, "E145.0.1.363", {"start": v(-17.66, -26.73) * mm, "end": v(-17.86, -27.18) * mm});
            skLineSegment(sketch, "E145.0.1.364", {"start": v(11.67, -19.38) * mm, "end": v(12.07, -19.68) * mm});
            skLineSegment(sketch, "E145.0.1.365", {"start": v(-9.97, -51.76) * mm, "end": v(-11.97, -55.22) * mm});
            skLineSegment(sketch, "E145.0.1.366", {"start": v(-19.4, -21.74) * mm, "end": v(-19.68, -22.15) * mm});
            skLineSegment(sketch, "E145.0.1.367", {"start": v(-12.56, -49.91) * mm, "end": v(-12.18, -50.23) * mm});
            skLineSegment(sketch, "E145.0.1.368", {"start": v(-17.92, -42.7) * mm, "end": v(-21.61, -44.22) * mm});
            skLineSegment(sketch, "E145.0.1.369", {"start": v(-18.1, -42.23) * mm, "end": v(-17.92, -42.7) * mm});
            skLineSegment(sketch, "E145.0.1.370", {"start": v(19.47, -36.03) * mm, "end": v(19.44, -36.52) * mm});
            skLineSegment(sketch, "E145.0.1.371", {"start": v(-16.07, -23.96) * mm, "end": v(-16.35, -24.38) * mm});
            skLineSegment(sketch, "E145.0.1.372", {"start": v(-11.67, -19.38) * mm, "end": v(-14.1, -16.2) * mm});
            skLineSegment(sketch, "E145.0.1.373", {"start": v(-2.93, -15.72) * mm, "end": v(-3.42, -15.8) * mm});
            skLineSegment(sketch, "E145.0.1.374", {"start": v(-21.8, -43.76) * mm, "end": v(-21.61, -44.22) * mm});
            skLineSegment(sketch, "E145.0.1.375", {"start": v(-11.97, -55.22) * mm, "end": v(-11.53, -55.47) * mm});
            skLineSegment(sketch, "E145.0.1.376", {"start": v(-9.53, -52.01) * mm, "end": v(-11.53, -55.47) * mm});
            skLineSegment(sketch, "E145.0.1.377", {"start": v(-19.38, -32.84) * mm, "end": v(-19.43, -33.34) * mm});
            skLineSegment(sketch, "E145.0.1.378", {"start": v(-16.07, -23.96) * mm, "end": v(-19.4, -21.74) * mm});
            skLineSegment(sketch, "E145.0.1.379", {"start": v(-15.15, -38.28) * mm, "end": v(-15.04, -38.76) * mm});
            skLineSegment(sketch, "E145.0.1.380", {"start": v(-16.35, -24.38) * mm, "end": v(-19.68, -22.15) * mm});
            skLineSegment(sketch, "E145.0.1.381", {"start": v(-9.53, -52.01) * mm, "end": v(-11.53, -55.47) * mm});
            skLineSegment(sketch, "E145.0.1.382", {"start": v(-17.66, -26.73) * mm, "end": v(-17.86, -27.18) * mm});
            skLineSegment(sketch, "E145.0.1.383", {"start": v(-15.15, -38.28) * mm, "end": v(-15.04, -38.76) * mm});
            skLineSegment(sketch, "E145.0.1.384", {"start": v(-18.9, -30.2) * mm, "end": v(-22.76, -29.16) * mm});
            skLineSegment(sketch, "E145.0.1.385", {"start": v(-16.07, -23.96) * mm, "end": v(-19.4, -21.74) * mm});
            skLineSegment(sketch, "E145.0.1.386", {"start": v(6.03, -16.46) * mm, "end": v(6.5, -16.62) * mm});
            skLineSegment(sketch, "E145.0.1.387", {"start": v(11.67, -19.38) * mm, "end": v(12.07, -19.68) * mm});
            skLineSegment(sketch, "E145.0.1.388", {"start": v(-19.05, -39.18) * mm, "end": v(-18.93, -39.67) * mm});
            skLineSegment(sketch, "E145.0.1.389", {"start": v(-11.67, -19.38) * mm, "end": v(-14.1, -16.2) * mm});
            skLineSegment(sketch, "E145.0.1.390", {"start": v(-18.1, -42.23) * mm, "end": v(-21.8, -43.76) * mm});
            skLineSegment(sketch, "E145.0.1.391", {"start": v(22.63, -28.68) * mm, "end": v(22.76, -29.16) * mm});
            skLineSegment(sketch, "E145.0.1.392", {"start": v(-9.97, -51.76) * mm, "end": v(-11.97, -55.22) * mm});
            skLineSegment(sketch, "E145.0.1.393", {"start": v(19.47, -36.03) * mm, "end": v(19.44, -36.52) * mm});
            skLineSegment(sketch, "E145.0.1.394", {"start": v(-12.07, -19.68) * mm, "end": v(-14.5, -16.5) * mm});
            skLineSegment(sketch, "E145.0.1.395", {"start": v(-17.92, -42.7) * mm, "end": v(-21.61, -44.22) * mm});
            skLineSegment(sketch, "E145.0.1.396", {"start": v(-18.77, -29.71) * mm, "end": v(-22.63, -28.68) * mm});
            skLineSegment(sketch, "E145.0.1.397", {"start": v(-18.1, -42.23) * mm, "end": v(-17.92, -42.7) * mm});
            skLineSegment(sketch, "E145.0.1.398", {"start": v(-16.07, -23.96) * mm, "end": v(-16.35, -24.38) * mm});
            skLineSegment(sketch, "E145.0.1.399", {"start": v(-11.97, -55.22) * mm, "end": v(-11.53, -55.47) * mm});
            skLineSegment(sketch, "E145.0.1.400", {"start": v(-12.56, -49.91) * mm, "end": v(-12.18, -50.23) * mm});
            skLineSegment(sketch, "E145.0.1.401", {"start": v(-9.97, -51.76) * mm, "end": v(-9.53, -52.01) * mm});
            skLineSegment(sketch, "E145.0.1.402", {"start": v(-21.8, -43.76) * mm, "end": v(-21.61, -44.22) * mm});
            skLineSegment(sketch, "E145.0.1.403", {"start": v(-14.1, -16.2) * mm, "end": v(-14.5, -16.5) * mm});
            skLineSegment(sketch, "E145.0.1.404", {"start": v(-18.77, -29.71) * mm, "end": v(-18.9, -30.2) * mm});
            skLineSegment(sketch, "E145.0.1.405", {"start": v(-19.38, -32.84) * mm, "end": v(-19.43, -33.34) * mm});
            skLineSegment(sketch, "E145.0.1.406", {"start": v(-19.4, -21.74) * mm, "end": v(-19.68, -22.15) * mm});
            skLineSegment(sketch, "E145.0.1.407", {"start": v(-2.93, -15.72) * mm, "end": v(-3.42, -15.8) * mm});
            skLineSegment(sketch, "E145.0.1.408", {"start": v(-2.93, -15.72) * mm, "end": v(-3.42, -15.8) * mm});
            skLineSegment(sketch, "E145.0.1.409", {"start": v(-12.56, -49.91) * mm, "end": v(-12.18, -50.23) * mm});
            skLineSegment(sketch, "E145.0.1.410", {"start": v(6.03, -16.46) * mm, "end": v(6.5, -16.62) * mm});
            skLineSegment(sketch, "E145.0.1.411", {"start": v(11.67, -19.38) * mm, "end": v(12.07, -19.68) * mm});
            skLineSegment(sketch, "E145.0.1.412", {"start": v(22.63, -28.68) * mm, "end": v(22.76, -29.16) * mm});
            skLineSegment(sketch, "E145.0.1.413", {"start": v(-17.66, -26.73) * mm, "end": v(-17.86, -27.18) * mm});
            skLineSegment(sketch, "E145.0.1.414", {"start": v(-19.05, -39.18) * mm, "end": v(-18.93, -39.67) * mm});
            skLineSegment(sketch, "E145.0.1.415", {"start": v(19.47, -36.03) * mm, "end": v(19.44, -36.52) * mm});
            skLineSegment(sketch, "E145.0.1.416", {"start": v(-18.9, -30.2) * mm, "end": v(-22.76, -29.16) * mm});
            skLineSegment(sketch, "E145.0.1.417", {"start": v(-18.77, -29.71) * mm, "end": v(-22.63, -28.68) * mm});
            skLineSegment(sketch, "E145.0.1.418", {"start": v(-21.8, -43.76) * mm, "end": v(-21.61, -44.22) * mm});
            skLineSegment(sketch, "E145.0.1.419", {"start": v(-18.1, -42.23) * mm, "end": v(-17.92, -42.7) * mm});
            skLineSegment(sketch, "E145.0.1.420", {"start": v(-11.97, -55.22) * mm, "end": v(-11.53, -55.47) * mm});
            skLineSegment(sketch, "E145.0.1.421", {"start": v(-16.07, -23.96) * mm, "end": v(-16.35, -24.38) * mm});
            skLineSegment(sketch, "E145.0.1.422", {"start": v(-14.1, -16.2) * mm, "end": v(-14.5, -16.5) * mm});
            skLineSegment(sketch, "E145.0.1.423", {"start": v(-18.77, -29.71) * mm, "end": v(-18.9, -30.2) * mm});
            skLineSegment(sketch, "E145.0.1.424", {"start": v(-19.4, -21.74) * mm, "end": v(-19.68, -22.15) * mm});
            skLineSegment(sketch, "E145.0.1.425", {"start": v(-9.97, -51.76) * mm, "end": v(-9.53, -52.01) * mm});
            skLineSegment(sketch, "E145.0.1.426", {"start": v(-18.1, -42.23) * mm, "end": v(-17.92, -42.7) * mm});
            skLineSegment(sketch, "E145.0.1.427", {"start": v(-19.4, -21.74) * mm, "end": v(-19.68, -22.15) * mm});
            skLineSegment(sketch, "E145.0.1.428", {"start": v(-2.93, -15.72) * mm, "end": v(-3.42, -15.8) * mm});
            skLineSegment(sketch, "E145.0.1.429", {"start": v(11.67, -19.38) * mm, "end": v(12.07, -19.68) * mm});
            skLineSegment(sketch, "E145.0.1.430", {"start": v(6.03, -16.46) * mm, "end": v(6.5, -16.62) * mm});
            skLineSegment(sketch, "E145.0.1.431", {"start": v(22.63, -28.68) * mm, "end": v(22.76, -29.16) * mm});
            skLineSegment(sketch, "E145.0.1.432", {"start": v(-19.05, -39.18) * mm, "end": v(-18.93, -39.67) * mm});
            skLineSegment(sketch, "E145.0.1.433", {"start": v(-12.56, -49.91) * mm, "end": v(-12.18, -50.23) * mm});
            skLineSegment(sketch, "E145.0.1.434", {"start": v(-17.66, -26.73) * mm, "end": v(-17.86, -27.18) * mm});
            skLineSegment(sketch, "E145.0.1.435", {"start": v(19.47, -36.03) * mm, "end": v(19.44, -36.52) * mm});
            skLineSegment(sketch, "E145.0.1.436", {"start": v(-21.8, -43.76) * mm, "end": v(-21.61, -44.22) * mm});
            skLineSegment(sketch, "E145.0.1.437", {"start": v(-9.97, -51.76) * mm, "end": v(-9.53, -52.01) * mm});
            skLineSegment(sketch, "E145.0.1.438", {"start": v(-16.07, -23.96) * mm, "end": v(-16.35, -24.38) * mm});
            skLineSegment(sketch, "E145.0.1.439", {"start": v(-11.97, -55.22) * mm, "end": v(-11.53, -55.47) * mm});
            skLineSegment(sketch, "E145.0.1.440", {"start": v(-18.77, -29.71) * mm, "end": v(-18.9, -30.2) * mm});
            skLineSegment(sketch, "E145.0.1.441", {"start": v(-6.03, -16.46) * mm, "end": v(-6.5, -16.62) * mm});
            skLineSegment(sketch, "E145.0.1.442", {"start": v(-14.1, -16.2) * mm, "end": v(-14.5, -16.5) * mm});
            skLineSegment(sketch, "E145.0.1.443", {"start": v(-21.8, -43.76) * mm, "end": v(-21.61, -44.22) * mm});
            skLineSegment(sketch, "E145.0.1.444", {"start": v(-9.97, -51.76) * mm, "end": v(-9.53, -52.01) * mm});
            skLineSegment(sketch, "E145.0.1.445", {"start": v(-14.1, -16.2) * mm, "end": v(-14.5, -16.5) * mm});
            skLineSegment(sketch, "E145.0.1.446", {"start": v(-11.97, -55.22) * mm, "end": v(-11.53, -55.47) * mm});
            skLineSegment(sketch, "E145.0.1.447", {"start": v(-18.1, -42.23) * mm, "end": v(-17.92, -42.7) * mm});
            skLineSegment(sketch, "E145.0.1.448", {"start": v(-18.77, -29.71) * mm, "end": v(-18.9, -30.2) * mm});
            skLineSegment(sketch, "E145.0.1.449", {"start": v(-16.07, -23.96) * mm, "end": v(-16.35, -24.38) * mm});
            skLineSegment(sketch, "E145.0.1.450", {"start": v(-6.03, -16.46) * mm, "end": v(-6.5, -16.62) * mm});
            skLineSegment(sketch, "E145.0.1.451", {"start": v(-14.1, -16.2) * mm, "end": v(-14.5, -16.5) * mm});
            skLineSegment(sketch, "E145.0.1.452", {"start": v(-21.8, -43.76) * mm, "end": v(-21.61, -44.22) * mm});
            skLineSegment(sketch, "E145.0.1.453", {"start": v(-9.97, -51.76) * mm, "end": v(-9.53, -52.01) * mm});
            skLineSegment(sketch, "E145.0.1.454", {"start": v(-11.97, -55.22) * mm, "end": v(-11.53, -55.47) * mm});
            skLineSegment(sketch, "E145.0.1.455", {"start": v(-18.1, -42.23) * mm, "end": v(-17.92, -42.7) * mm});
            skLineSegment(sketch, "E145.0.1.456", {"start": v(-6.03, -16.46) * mm, "end": v(-6.5, -16.62) * mm});
            skLineSegment(sketch, "E145.0.1.457", {"start": v(-16.07, -23.96) * mm, "end": v(-16.35, -24.38) * mm});
            skLineSegment(sketch, "E145.0.1.458", {"start": v(-18.77, -29.71) * mm, "end": v(-18.9, -30.2) * mm});
            skLineSegment(sketch, "E145.0.1.459", {"start": v(-18.77, -29.71) * mm, "end": v(-18.9, -30.2) * mm});
            skLineSegment(sketch, "E145.0.1.460", {"start": v(-9.97, -51.76) * mm, "end": v(-9.53, -52.01) * mm});
            skLineSegment(sketch, "E145.0.1.461", {"start": v(-14.1, -16.2) * mm, "end": v(-14.5, -16.5) * mm});
            skLineSegment(sketch, "E145.0.1.462", {"start": v(-16.07, -23.96) * mm, "end": v(-16.35, -24.38) * mm});
            skLineSegment(sketch, "E145.0.1.463", {"start": v(-21.8, -43.76) * mm, "end": v(-21.61, -44.22) * mm});
            skLineSegment(sketch, "E145.0.1.464", {"start": v(-18.1, -42.23) * mm, "end": v(-17.92, -42.7) * mm});
            skLineSegment(sketch, "E145.0.1.465", {"start": v(-11.97, -55.22) * mm, "end": v(-11.53, -55.47) * mm});
            skLineSegment(sketch, "E145.0.1.466", {"start": v(-6.03, -16.46) * mm, "end": v(-6.5, -16.62) * mm});
            skLineSegment(sketch, "E145.0.1.467", {"start": v(-18.77, -29.71) * mm, "end": v(-18.9, -30.2) * mm});
            skLineSegment(sketch, "E145.0.1.468", {"start": v(-6.03, -16.46) * mm, "end": v(-6.5, -16.62) * mm});
            skLineSegment(sketch, "E145.0.1.469", {"start": v(-14.1, -16.2) * mm, "end": v(-14.5, -16.5) * mm});
            skLineSegment(sketch, "E145.0.1.470", {"start": v(-16.07, -23.96) * mm, "end": v(-16.35, -24.38) * mm});
            skLineSegment(sketch, "E145.0.1.471", {"start": v(-18.1, -42.23) * mm, "end": v(-17.92, -42.7) * mm});
            skLineSegment(sketch, "E145.0.1.472", {"start": v(-21.8, -43.76) * mm, "end": v(-21.61, -44.22) * mm});
            skLineSegment(sketch, "E145.0.1.473", {"start": v(-9.97, -51.76) * mm, "end": v(-9.53, -52.01) * mm});
            skLineSegment(sketch, "E145.0.1.474", {"start": v(-11.97, -55.22) * mm, "end": v(-11.53, -55.47) * mm});
            skLineSegment(sketch, "E145.0.1.475", {"start": v(-6.03, -16.46) * mm, "end": v(-6.5, -16.62) * mm});
            skLineSegment(sketch, "E145.0.1.476", {"start": v(-14.1, -16.2) * mm, "end": v(-14.5, -16.5) * mm});
            skLineSegment(sketch, "E145.0.1.477", {"start": v(-9.97, -51.76) * mm, "end": v(-9.53, -52.01) * mm});
            skLineSegment(sketch, "E145.0.1.478", {"start": v(-18.77, -29.71) * mm, "end": v(-18.9, -30.2) * mm});
            skLineSegment(sketch, "E145.0.1.479", {"start": v(-6.03, -16.46) * mm, "end": v(-6.5, -16.62) * mm});
            skLineSegment(sketch, "E145.0.1.480", {"start": v(-6.03, -16.46) * mm, "end": v(-6.5, -16.62) * mm});
            skLineSegment(sketch, "E145.0.1.481", {"start": v(-11.67, -19.38) * mm, "end": v(-12.07, -19.68) * mm});
            skLineSegment(sketch, "E145.0.1.482", {"start": v(-19.47, -36.03) * mm, "end": v(-19.44, -36.52) * mm});
            skLineSegment(sketch, "E145.0.1.483", {"start": v(-22.63, -28.68) * mm, "end": v(-22.76, -29.16) * mm});
            skLineSegment(sketch, "E145.0.1.484", {"start": v(-14.82, -47.67) * mm, "end": v(-14.5, -48.04) * mm});
            skLineSegment(sketch, "E145.0.1.485", {"start": v(-19.47, -36.03) * mm, "end": v(-19.44, -36.52) * mm});
            skLineSegment(sketch, "E145.0.1.486", {"start": v(-22.63, -28.68) * mm, "end": v(-22.76, -29.16) * mm});
            skLineSegment(sketch, "E145.0.1.487", {"start": v(-14.82, -47.67) * mm, "end": v(-14.5, -48.04) * mm});
            skLineSegment(sketch, "E145.0.1.488", {"start": v(-11.67, -19.38) * mm, "end": v(-12.07, -19.68) * mm});
            skLineSegment(sketch, "E145.0.1.489", {"start": v(-19.47, -36.03) * mm, "end": v(-19.44, -36.52) * mm});
            skLineSegment(sketch, "E145.0.1.490", {"start": v(-22.63, -28.68) * mm, "end": v(-22.76, -29.16) * mm});
            skLineSegment(sketch, "E145.0.1.491", {"start": v(-14.82, -47.67) * mm, "end": v(-14.5, -48.04) * mm});
            skLineSegment(sketch, "E145.0.1.492", {"start": v(-11.67, -19.38) * mm, "end": v(-12.07, -19.68) * mm});
            skLineSegment(sketch, "E145.0.1.493", {"start": v(-19.47, -36.03) * mm, "end": v(-19.44, -36.52) * mm});
            skLineSegment(sketch, "E145.0.1.494", {"start": v(-22.63, -28.68) * mm, "end": v(-22.76, -29.16) * mm});
            skLineSegment(sketch, "E145.0.1.495", {"start": v(-14.82, -47.67) * mm, "end": v(-14.5, -48.04) * mm});
            skLineSegment(sketch, "E145.0.1.496", {"start": v(-11.67, -19.38) * mm, "end": v(-12.07, -19.68) * mm});
            skLineSegment(sketch, "E145.0.1.497", {"start": v(-22.63, -28.68) * mm, "end": v(-22.76, -29.16) * mm});
            skLineSegment(sketch, "E145.0.1.498", {"start": v(-19.47, -36.03) * mm, "end": v(-19.44, -36.52) * mm});
            skLineSegment(sketch, "E145.0.1.499", {"start": v(-11.67, -19.38) * mm, "end": v(-12.07, -19.68) * mm});
            skLineSegment(sketch, "E145.0.1.500", {"start": v(-14.82, -47.67) * mm, "end": v(-14.5, -48.04) * mm});
            skLineSegment(sketch, "E145.0.1.501", {"start": v(-22.63, -28.68) * mm, "end": v(-22.76, -29.16) * mm});
            skLineSegment(sketch, "E145.0.1.502", {"start": v(-11.67, -19.38) * mm, "end": v(-12.07, -19.68) * mm});
            skLineSegment(sketch, "E145.0.1.503", {"start": v(-19.47, -36.03) * mm, "end": v(-19.44, -36.52) * mm});
            skLineSegment(sketch, "E145.0.1.504", {"start": v(-14.82, -47.67) * mm, "end": v(-14.5, -48.04) * mm});
            skLineSegment(sketch, "E145.0.1.505", {"start": v(-14.82, -47.67) * mm, "end": v(-14.5, -48.04) * mm});
            skLineSegment(sketch, "E145.0.1.506", {"start": v(-22.63, -28.68) * mm, "end": v(-22.76, -29.16) * mm});
            skLineSegment(sketch, "E145.0.1.507", {"start": v(-11.67, -19.38) * mm, "end": v(-12.07, -19.68) * mm});
            skLineSegment(sketch, "E145.0.1.508", {"start": v(-19.47, -36.03) * mm, "end": v(-19.44, -36.52) * mm});
            skLineSegment(sketch, "E145.0.1.509", {"start": v(-22.63, -28.68) * mm, "end": v(-22.76, -29.16) * mm});
            skLineSegment(sketch, "E145.0.1.510", {"start": v(-11.67, -19.38) * mm, "end": v(-12.07, -19.68) * mm});
            skLineSegment(sketch, "E145.0.1.511", {"start": v(-19.47, -36.03) * mm, "end": v(-19.44, -36.52) * mm});
            skLineSegment(sketch, "E145.0.1.512", {"start": v(-14.82, -47.67) * mm, "end": v(-14.5, -48.04) * mm});
            skLineSegment(sketch, "E145.direction1", {"start": v(-13.97, -8.69) * mm, "end": v(13.97, -8.69) * mm, "construction": true});
            skLineSegment(sketch, "E145.direction2", {"start": v(-13.97, -8.69) * mm, "end": v(-13.97, -58.69) * mm, "construction": true});
            skSolve(sketch);
        }
        {
            var Q0;
            Q0 = qSketchRegion(id + "F8", true);
            extrude(context, id + "F9", {"entities" : qUnion([Q0]), "operationType" : NewBodyOperationType.REMOVE, "oppositeDirection" : true, "depth" : 1 * mm});
        }
    });
